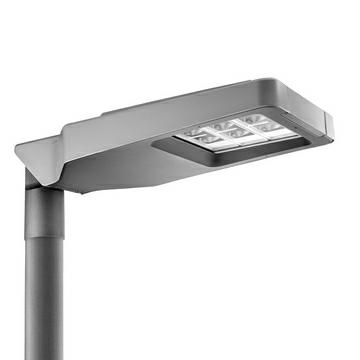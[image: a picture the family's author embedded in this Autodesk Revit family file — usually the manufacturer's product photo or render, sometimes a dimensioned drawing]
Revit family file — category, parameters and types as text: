
# Revit family: Lighting-StreetLighting-GEWISS-ROAD[5]MEDIUM-LED_OPTIC_HUGE_CLII
name_source: partatom
category: Apparecchi per illuminazione
units: mm (PartAtom-declared; Revit-internal decimal feet)

## family parameters
Basato su piano di lavoro = No
Condiviso = No
Punto di calcolo locali = No
Quota connettore circolare = Usa diametro
Sempre verticale = Sì
Sorgente d'illuminazione = No
Taglio con vuoti quando caricato = No
Tipo di parte = Normale

## types (65) — shared parameters
Applicazione = External
Catalogue = LIGHTING
IDF = edd43bf0-fde5-4ceb-9c5d-851512cf025d
IDT = ab01e1b5e8824c1da94a21a5ceb91f42
IP degree = IP66
Immagine tipo = GWR5276M.jpg
Insulation class = II
Lampada = LED
Produttore = GEWISS S.p.A.
Shock resistance = IK08
Technical sheet = https://www.gewiss.com
URL = https://www.gewiss.com
Version file RFA = 20.11
Warranty = 5 years

## per-type parameters (varying)
- GWR5174B - ROAD5 MEDI HUGE 4M 4000K 0,7A CL2 BIREG: Catalogue Range=ROAD [5]; Colour temperature=4000 K (CRI 70); Colour temperature:=4000 K (CRI 70); Descrizione=ROAD 5 BI-POW.4M 4000K 700mA OPT.ST1; EAN code=8011564858022; Electrocod=244C; LED LifeTime (L80B05)=77000H; LED current.=0,7A; Lamp-=LED; Lumen output (lm)=9190; Maximum surface exposed to the wind=0,19M2; Minimum distance from the illuminated object=1M; Modello=GWR5174B; No. Chorus modules=4 (4x3 LED); Nominal flux (lm)=12480; Number of modules=4 (4x3 LED); Operating temperature:=-25 +50 °C; Optic=H - ULOR: 0%; Overvoltage resistance=12 KV (Common and dfferential mode); Pilot current=0,7A; Power supply operation=Bi power; SEO=Street lighting; System power=108W; Tilt adjustable=-20° ÷ +10° side bracket - -10° ÷ +20° pole head; Tipo alimentatore=Constant Current Driver Led; Tipologia=Bi power; Voltage-=220/240 V - 50/60 Hz - Bi-power with self-learning; Weight (kg)=8,4; Weight (kg):=8,4; Working temperature=-25 +50 °C
- GWR5116B - ROAD5 MEDI HUGE 6M 4000K 0,85A CL2 BIREG: Catalogue Range=ROAD [5]; Colour temperature=4000 K (CRI 70); Colour temperature:=4000 K (CRI 70); Descrizione=ROAD 5 BI-POW.6M 4000K 0,85A OPT.ST1; EAN code=8011564858077; Electrocod=244C; LED LifeTime (L80B05)=120000H; LED current.=0,85A; Lamp-=LED; Lumen output (lm)=17160; Maximum surface exposed to the wind=0,19M2; Minimum distance from the illuminated object=1M; Modello=GWR5116B; No. Chorus modules=6 (6x3 LED); Nominal flux (lm)=24330; Number of modules=6 (6x3 LED); Operating temperature:=-25 +40 °C; Optic=H - ULOR: 0%; Overvoltage resistance=12 KV (Common and dfferential mode); Pilot current=0,85A; Power supply operation=Bi power; SEO=Street lighting; System power=187W; Tilt adjustable=-20° ÷ +10° side bracket - -10° ÷ +20° pole head; Tipo alimentatore=Constant Current Driver Led; Tipologia=Bi power; Voltage-=220/240 V - 50/60 Hz - Bi-power with self-learning; Weight (kg)=9.1; Weight (kg):=9,1; Working temperature=-25 +40 °C
- GWR511530K - ROAD5 MEDI HUGE 5M 3000K 0,85A CL2: Body=Die-cast aluminium -; Catalogue Range=ROAD [5]; Classification:=-; Color Rendering Index=CRI-70; Colore=Graphite grey; Colour :=Powder coating; Colour temperature=3000K; Colour temperature:=3000 K (CRI>80); Context=Street and parking lighting; Control System=Stand alone; DIN 18032-3 certification=-; Descrizione=GWR511530K - ROAD5 MEDI HUGE 5M 3000K 0,85A CL2; Device with reduced surface temperature=-; Driver=Included; Driver Box=Built-in; Efficiency (lm/W)=96; Electrocod=244C; Eletrical and lighting features=-; External screw=Stainless steel; Fixing=Pole Head - Outreach; Gasket=Anti-aging silicone; General information=-; Glow Wire Test :=-; IPEA=ROAD = B // LARGE AREAS = A ++ // CYCLOPEDONALS = B // GREEN AREAS = B // HISTORICAL CENTER = A3 +; Installationa and maintenance=-; LED Life Time (L80B05)=120000H; LED Maintenance=Not available; LED current.=0,849999999999999A; Lamp-=LED; Lifetime=L90B10 (Tq+25°C) = 100.000 h - L90B10 (Tq+40°C) = 50.000 h; Locking Hook=Integrated front handle; Lumen output (lm)=15300; Luminaire=LED Road Equipment; Materials=-; Maximum surface exposed to the wind=0,19M2; Maximum surface exposed to the wind :=0.19 m2; Minimum distance from the illuminated object=1M; Modello=GWR511530K; Mouting and installation=Pole Head - Outreach; Nominal flux (lm)=18423; Number of modules=5 (5x3 LED); Operating temperature :=-25 +40 °C; Operating temperature:=-25 +40 °C; Optic=HUGE; Optic :=Metallized polycarbonate reflector; Optic Maintenance=Not available; Optic and illuminating features=-; Overvoltage protection=DM 10KV / CM 10KV; Overvoltage resistance :=Common and dfferential mode: 10KV; Photobiological Risk Class=RG0; Rated frequency (Hz)=50 / 60; SEO=Street lighting; Shield type=4mm thick flat tempered glass; Standard Deviation Colour Matching=SDCM = 5; Standard-=EN 60598-2-3, EN 60598-1 IEC/TR 62778; Standards and approvals=-; Stocking temperature=-; Supply voltage=220 - 240 V; System power=159W; System power :=159 W @ 0.85A; Tilt adjustable=-20° ÷ +10° side bracket - -10° ÷ +20° pole head; Tilt-=-20° ÷ +10° side bracket - -10° ÷ +20° pole head; Tipo alimentatore=Constant Current Driver Led; Tipologia=Stand alone; Type of light source=LED - Not replaceable; Unified Glare Rating=G*3 - ULOR = 0; Unique digital code (Datamatrix)=Currently not present; Voltage-=220/240 V - 50/60 Hz - Stand alone; Weight (kg):=8,8; Wiring=Isolating switch
- GWR5174 - ROAD5 MEDI HUGE 4M 4000K 0,7A CL2: Catalogue Range=ROAD [5]; Colour temperature=4000 K (CRI 70); Colour temperature:=4000 K (CRI 70); Descrizione=ROAD 5 4M 4000K 700mA OPT.ST1; EAN code=8011564857940; Electrocod=244C; LED LifeTime (L80B05)=77000H; LED current.=0,7A; Lamp-=LED; Lumen output (lm)=9190; Maximum surface exposed to the wind=0,19M2; Minimum distance from the illuminated object=1M; Modello=GWR5174; No. Chorus modules=4 (4x3 LED); Nominal flux (lm)=12480; Number of modules=4 (4x3 LED); Operating temperature:=-25 +50 °C; Optic=H - ULOR: 0%; Overvoltage resistance=12 KV (Common and dfferential mode); Pilot current=0,7A; SEO=Street lighting; System power=106W; Tilt adjustable=-20° ÷ +10° side bracket - -10° ÷ +20° pole head; Tipo alimentatore=Constant Current Driver Led; Tipologia=Stand alone; Voltage-=220/240 V - 50/60 Hz - Stand alone; Weight (kg)=8,4; Weight (kg):=8,4; Working temperature=-25 +50 °C
- GWR5155B - ROAD5 MEDI HUGE 5M 4000K 0,5A CL2 BIREG: Body=Die-cast aluminium -; Catalogue Range=ROAD [5]; Classification:=-; Color Rendering Index=CRI-70; Colore=Graphite grey; Colour :=Powder coating; Colour temperature=4000K; Colour temperature:=4000 K (CRI>70); Context=Street and parking lighting; Control System=Bi-power with self-learning; DIN 18032-3 certification=-; Descrizione=GWR5155B - ROAD5 MEDI HUGE 5M 4000K 0,5A CL2 BIREG; Device with reduced surface temperature=-; Driver=Included; Driver Box=Built-in; Efficiency (lm/W)=117; Electrocod=244C; Eletrical and lighting features=-; External screw=Stainless steel; Fixing=Pole Head - Outreach; Gasket=Anti-aging silicone; General information=-; Glow Wire Test :=-; IPEA=ROAD = A3 + // LARGE AREAS = A5 + // CYCLOPEDONALS = A ++ // GREEN AREAS = A ++ // HISTORICAL CENTER = A6 +; Installationa and maintenance=-; LED Life Time (L80B05)=120000H; LED Maintenance=Not available; LED current.=0,5A; Lamp-=LED; Lifetime=L90B10 (Tq+25°C) = 100.000 h - L90B10 (Tq+50°C) = 50.000 h; Locking Hook=Integrated front handle; Lumen output (lm)=11000; Luminaire=LED Road Equipment; Materials=-; Maximum surface exposed to the wind=0,19M2; Maximum surface exposed to the wind :=0.19 m2; Minimum distance from the illuminated object=1M; Modello=GWR5155B; Mouting and installation=Pole Head - Outreach; Nominal flux (lm)=12000; Number of modules=5 (5x3 LED); Operating temperature :=-25 +50 °C; Operating temperature:=-25 +40 °C; Optic=HUGE; Optic :=Metallized polycarbonate reflector; Optic Maintenance=Not available; Optic and illuminating features=-; Overvoltage protection=DM 10KV / CM 10KV; Photobiological Risk Class=RG0; Power supply operation=Bi power; Rated frequency (Hz)=50 / 60; SEO=Street lighting; Shield type=4mm thick flat tempered glass; Standard Deviation Colour Matching=SDCM = 5; Standard-=EN 60598-2-3, EN 60598-1 IEC/TR 62778; Standards and approvals=-; Stocking temperature=-; Supply voltage=220 - 240 V; System power=91W; System power :=94 W @ 0.5A; Tilt adjustable=-20° ÷ +10° side bracket - -10° ÷ +20° pole head; Tilt-=-20° ÷ +10° side bracket - -10° ÷ +20° pole head; Type of light source=LED - Not replaceable; Unified Glare Rating=G*3 - ULOR = 0; Unique digital code (Datamatrix)=Currently not present; Voltage-=220/240 V - 50/60 Hz - Bi-power with self-learning; Weight (kg):=8,8; Wiring=Isolating switch
- GWR5176M - ROAD5 MEDI HUGE 6M 4000K 0,7A CL2 1-10V: Catalogue Range=ROAD [5]; Colour temperature=4000 K (CRI 70); Colour temperature:=4000 K (CRI 70); Descrizione=ROAD 5 DIMM.6M 4000K 700mA OPT.ST1; EAN code=8011564858244; Electrocod=244C; LED LifeTime (L80B05)=77000H; LED current.=0,7A; Lamp-=LED; Lumen output (lm)=13780; Maximum surface exposed to the wind=0,19M2; Minimum distance from the illuminated object=1M; Modello=GWR5176M; No. Chorus modules=6 (6x3 LED); Nominal flux (lm)=18720; Number of modules=6 (6x3 LED); Operating temperature:=-25 +50 °C; Optic=H - ULOR: 0%; Overvoltage resistance=12 KV (Common and dfferential mode); Pilot current=0,7A; Power supply operation=Dimmable; SEO=Street lighting; System power=159W; Tilt adjustable=-20° ÷ +10° side bracket - -10° ÷ +20° pole head; Tipo alimentatore=Constant Current Driver Led; Tipologia=Dimmable; Voltage-=220/240 V - 50/60 Hz - Dimmable 1-10 V; Weight (kg)=9.1; Weight (kg):=9,1; Working temperature=-25 +50 °C
- GWR5113B30K - ROAD5 MEDI HUGE 3M 3000K 1,0A CL2 BIREG: Body=Die-cast aluminium -; Catalogue Range=ROAD [5]; Classification:=-; Color Rendering Index=CRI-70; Colore=Graphite grey; Colour :=Powder coating; Colour temperature=3000K; Colour temperature:=3000 K (CRI>80); Context=Street and parking lighting; Control System=Bi-power with self-learning; DIN 18032-3 certification=-; Descrizione=GWR5113B30K - ROAD5 MEDI HUGE 3M 3000K 1,0A CL2 BIREG; Device with reduced surface temperature=-; Driver=Included; Driver Box=Built-in; Efficiency (lm/W)=91; Electrocod=244C; Eletrical and lighting features=-; External screw=Stainless steel; Fixing=Pole Head - Outreach; Gasket=Anti-aging silicone; General information=-; Glow Wire Test :=-; IPEA=ROAD = A // LARGE AREAS = A ++ // CYCLOPEDONALS = B // GREEN AREAS = B // HISTORICAL CENTER = A3 +; Installationa and maintenance=-; LED Life Time (L80B05)=120000H; LED Maintenance=Not available; LED current.=1A; Lamp-=LED; Lifetime=L90B10 (Tq+25°C) = 100.000 h - L90B10 (Tq+40°C) = 75.000 h; Locking Hook=Integrated front handle; Lumen output (lm)=10500; Luminaire=LED Road Equipment; Materials=-; Maximum surface exposed to the wind=0,19M2; Maximum surface exposed to the wind :=0.19 m2; Minimum distance from the illuminated object=1M; Modello=GWR5113B30K; Mouting and installation=Pole Head - Outreach; Nominal flux (lm)=12420; Number of modules=3 (3x3 LED); Operating temperature :=-25 +40 °C; Operating temperature:=-25 +40 °C; Optic=HUGE; Optic :=Metallized polycarbonate reflector; Optic Maintenance=Not available; Optic and illuminating features=-; Overvoltage protection=DM 10KV / CM 10KV; Overvoltage resistance :=Common and dfferential mode: 10KV; Photobiological Risk Class=RG0; Power supply operation=Bi power; Rated frequency (Hz)=50 / 60; SEO=Street lighting; Shield type=4mm thick flat tempered glass; Standard Deviation Colour Matching=SDCM = 5; Standard-=EN 60598-2-3, EN 60598-1 IEC/TR 62778; Standards and approvals=-; Stocking temperature=-; Supply voltage=220 - 240 V; System power=115W; System power :=115 W @ 1A; Tilt adjustable=-20° ÷ +10° side bracket - -10° ÷ +20° pole head; Tilt-=-20° ÷ +10° side bracket - -10° ÷ +20° pole head; Tipo alimentatore=Constant Current Driver Led; Tipologia=Bi power; Type of light source=LED - Not replaceable; Unified Glare Rating=G*3 - ULOR = 0; Unique digital code (Datamatrix)=Currently not present; Voltage-=220/240 V - 50/60 Hz - Bi-power with self-learning; Weight (kg):=8; Wiring=Isolating switch
- GWR511630K - ROAD5 MEDI HUGE 6M 3000K 0,85A CL2: Body=Die-cast aluminium -; Catalogue Range=ROAD [5]; Classification:=-; Color Rendering Index=CRI-70; Colore=Graphite grey; Colour :=Powder coating; Colour temperature=3000K; Colour temperature:=3000 K (CRI>80); Context=Street and parking lighting; Control System=Stand alone; DIN 18032-3 certification=-; Descrizione=GWR511630K - ROAD5 MEDI HUGE 6M 3000K 0,85A CL2; Device with reduced surface temperature=-; Driver=Included; Driver Box=Built-in; Efficiency (lm/W)=99; Electrocod=244C; Eletrical and lighting features=-; External screw=Stainless steel; Fixing=Pole Head - Outreach; Gasket=Anti-aging silicone; General information=-; Glow Wire Test :=-; IPEA=ROAD = B // LARGE AREAS = A ++ // CYCLOPEDONALS = A // GREEN AREAS = A // HISTORICAL CENTER = A3 +; Installationa and maintenance=-; LED Life Time (L80B05)=120000H; LED Maintenance=Not available; LED current.=0,849999999999999A; Lamp-=LED; Lifetime=L90B10 (Tq+25°C) = 100.000 h - L90B10 (Tq+40°C) = 50.000 h; Locking Hook=Integrated front handle; Lumen output (lm)=18400; Luminaire=LED Road Equipment; Materials=-; Maximum surface exposed to the wind=0,19M2; Maximum surface exposed to the wind :=0.19 m2; Minimum distance from the illuminated object=1M; Modello=GWR511630K; Mouting and installation=Pole Head - Outreach; Nominal flux (lm)=21114; Number of modules=6 (6x3 LED); Operating temperature :=-25 +40 °C; Operating temperature:=-25 +40 °C; Optic=HUGE; Optic :=Metallized polycarbonate reflector; Optic Maintenance=Not available; Optic and illuminating features=-; Overvoltage protection=DM 10KV / CM 10KV; Overvoltage resistance :=Common and dfferential mode: 10KV; Photobiological Risk Class=RG0; Rated frequency (Hz)=50 / 60; SEO=Street lighting; Shield type=4mm thick flat tempered glass; Standard Deviation Colour Matching=SDCM = 5; Standard-=EN 60598-2-3, EN 60598-1 IEC/TR 62778; Standards and approvals=-; Stocking temperature=-; Supply voltage=220 - 240 V; System power=185W; System power :=185 W @ 0.85A; Tilt adjustable=-20° ÷ +10° side bracket - -10° ÷ +20° pole head; Tilt-=-20° ÷ +10° side bracket - -10° ÷ +20° pole head; Tipo alimentatore=Constant Current Driver Led; Tipologia=Stand alone; Type of light source=LED - Not replaceable; Unified Glare Rating=G*3 - ULOR = 0; Unique digital code (Datamatrix)=Currently not present; Voltage-=220/240 V - 50/60 Hz - Stand alone; Weight (kg):=9,09999999999999; Wiring=Isolating switch
- GWR5114B - ROAD5 MEDI HUGE 4M 4000K 1,0A CL2 BIREG: Catalogue Range=ROAD [5]; Colour temperature=4000 K (CRI 70); Colour temperature:=4000 K (CRI 70); Descrizione=ROAD 5 BI-POW.4M 4000K 1A OPT.ST1; EAN code=8011564858039; Electrocod=244C; LED LifeTime (L80B05)=120000H; LED current.=1A; Lamp-=LED; Lumen output (lm)=13460; Maximum surface exposed to the wind=0,19M2; Minimum distance from the illuminated object=1M; Modello=GWR5114B; No. Chorus modules=4 (4x3 LED); Nominal flux (lm)=19080; Number of modules=4 (4x3 LED); Operating temperature:=-25 +40 °C; Optic=H - ULOR: 0%; Overvoltage resistance=12 KV (Common and dfferential mode); Pilot current=1A; Power supply operation=Bi power; SEO=Street lighting; System power=153W; Tilt adjustable=-20° ÷ +10° side bracket - -10° ÷ +20° pole head; Tipo alimentatore=Constant Current Driver Led; Tipologia=Bi power; Voltage-=220/240 V - 50/60 Hz - Bi-power with self-learning; Weight (kg)=8,4; Weight (kg):=8,4; Working temperature=-25 +40 °C
- GWR5175 - ROAD5 MEDI HUGE 5M 4000K 0,7A CL2: Catalogue Range=ROAD [5]; Colour temperature=4000 K (CRI 70); Colour temperature:=4000 K (CRI 70); Descrizione=ROAD 5 5M 4000K 700mA OPT.ST1; EAN code=8011564857964; Electrocod=244C; LED LifeTime (L80B05)=77000H; LED current.=0,7A; Lamp-=LED; Lumen output (lm)=11480; Maximum surface exposed to the wind=0,19M2; Minimum distance from the illuminated object=1M; Modello=GWR5175; No. Chorus modules=5 (5x3 LED); Nominal flux (lm)=15600; Number of modules=5 (5x3 LED); Operating temperature:=-25 +50 °C; Optic=H - ULOR: 0%; Overvoltage resistance=12 KV (Common and dfferential mode); Pilot current=0,7A; SEO=Street lighting; System power=132W; Tilt adjustable=-20° ÷ +10° side bracket - -10° ÷ +20° pole head; Tipo alimentatore=Constant Current Driver Led; Tipologia=Stand alone; Voltage-=220/240 V - 50/60 Hz - Stand alone; Weight (kg)=8,8; Weight (kg):=8,8; Working temperature=-25 +50 °C
- GWR5156M - ROAD5 MEDI HUGE 6M 4000K 0,5A CL2 1-10V: Body=Die-cast aluminium -; Catalogue Range=ROAD [5]; Classification:=-; Color Rendering Index=CRI-70; Colore=Graphite grey; Colour :=Powder coating; Colour temperature=4000K; Colour temperature:=4000 K (CRI>70); Context=Street and parking lighting; Control System=Dimmable 1-10 V; DIN 18032-3 certification=-; Descrizione=GWR5156M - ROAD5 MEDI HUGE 6M 4000K 0,5A CL2 1-10V; Device with reduced surface temperature=-; Driver=Included; Driver Box=Built-in; Efficiency (lm/W)=117; Electrocod=244C; Eletrical and lighting features=-; External screw=Stainless steel; Fixing=Pole Head - Outreach; Gasket=Anti-aging silicone; General information=-; Glow Wire Test :=-; IPEA=ROAD = A3 + // LARGE AREAS = A5 + // CYCLOPEDONALS = A ++ // GREEN AREAS = A ++ // HISTORICAL CENTER = A6 +; Installationa and maintenance=-; LED Life Time (L80B05)=120000H; LED Maintenance=Not available; LED current.=0,5A; Lamp-=LED; Lifetime=L90B10 (Tq+25°C) = 100.000 h - L90B10 (Tq+50°C) = 50.000 h; Locking Hook=Integrated front handle; Lumen output (lm)=13200; Luminaire=LED Road Equipment; Materials=-; Maximum surface exposed to the wind=0,19M2; Maximum surface exposed to the wind :=0.19 m2; Minimum distance from the illuminated object=1M; Modello=GWR5156M; Mouting and installation=Pole Head - Outreach; Nominal flux (lm)=14400; Number of modules=6 (6x3 LED); Operating temperature :=-25 +50 °C; Operating temperature:=-25 +40 °C; Optic=HUGE; Optic :=Metallized polycarbonate reflector; Optic Maintenance=Not available; Optic and illuminating features=-; Overvoltage protection=DM 10KV / CM 10KV; Photobiological Risk Class=RG0; Rated frequency (Hz)=50 / 60; SEO=Street lighting; Shield type=4mm thick flat tempered glass; Standard Deviation Colour Matching=SDCM = 5; Standard-=EN 60598-2-3, EN 60598-1 IEC/TR 62778; Standards and approvals=-; Stocking temperature=-; Supply voltage=220 - 240 V; System power=109W; System power :=113 W @ 0.5A; Tilt adjustable=-20° ÷ +10° side bracket - -10° ÷ +20° pole head; Tilt-=-20° ÷ +10° side bracket - -10° ÷ +20° pole head; Tipologia=Dimmable; Type of light source=LED - Not replaceable; Unified Glare Rating=G*3 - ULOR = 0; Unique digital code (Datamatrix)=Currently not present; Voltage-=220/240 V - 50/60 Hz - Dimmable 1-10 V; Weight (kg):=9,09999999999999; Wiring=Isolating switch
- GWR5173M - ROAD5 MEDI HUGE 3M 4000K 0,7A CL2 1-10V: Catalogue Range=ROAD [5]; Colour temperature=4000 K (CRI 70); Colour temperature:=4000 K (CRI 70); Descrizione=ROAD 5 DIMM.3M 4000K 700mA OPT.ST1; EAN code=8011564858084; Electrocod=244C; LED LifeTime (L80B05)=77000H; LED current.=0,7A; Lamp-=LED; Lumen output (lm)=6890; Maximum surface exposed to the wind=0,19M2; Minimum distance from the illuminated object=1M; Modello=GWR5173M; No. Chorus modules=3 (3x3 LED); Nominal flux (lm)=9360; Number of modules=3 (3x3 LED); Operating temperature:=-25 +50 °C; Optic=H - ULOR: 0%; Overvoltage resistance=12 KV (Common and dfferential mode); Pilot current=0,7A; Power supply operation=Dimmable; SEO=Street lighting; System power=79W; Tilt adjustable=-20° ÷ +10° side bracket - -10° ÷ +20° pole head; Tipo alimentatore=Constant Current Driver Led; Tipologia=Dimmable; Voltage-=220/240 V - 50/60 Hz - Dimmable 1-10 V; Weight (kg)=8; Weight (kg):=8; Working temperature=-25 +50 °C
- GWR5174M30K - ROAD5 MEDI HUGE 4M 3000K 0,7A CL2 1-10V: Body=Die-cast aluminium -; Catalogue Range=ROAD [5]; Classification:=-; Color Rendering Index=CRI-70; Colore=Graphite grey; Colour :=Powder coating; Colour temperature=3000K; Colour temperature:=3000 K (CRI>80); Context=Street and parking lighting; Control System=Dimmable 1-10 V; DIN 18032-3 certification=-; Descrizione=GWR5174M30K - ROAD5 MEDI HUGE 4M 3000K 0,7A CL2 1-10V; Device with reduced surface temperature=-; Driver=Included; Driver Box=Built-in; Efficiency (lm/W)=96; Electrocod=244C; Eletrical and lighting features=-; External screw=Stainless steel; Fixing=Pole Head - Outreach; Gasket=Anti-aging silicone; General information=-; Glow Wire Test :=-; IPEA=ROAD = A // LARGE AREAS = A ++ // CYCLOPEDONALS = A // GREEN AREAS = A // HISTORICAL CENTER = A3 +; Installationa and maintenance=-; LED Life Time (L80B05)=77000H; LED Maintenance=Not available; LED current.=0,7A; Lamp-=LED; Lifetime=L90B10 (Tq+25°C) = 100.000 h - L90B10 (Tq+50°C) = 50.000 h; Locking Hook=Integrated front handle; Lumen output (lm)=10400; Luminaire=LED Road Equipment; Materials=-; Maximum surface exposed to the wind=0,19M2; Maximum surface exposed to the wind :=0.19 m2; Minimum distance from the illuminated object=1M; Modello=GWR5174M30K; Mouting and installation=Pole Head - Outreach; Nominal flux (lm)=10800; Number of modules=4 (4x3 LED); Operating temperature :=-25 +50 °C; Operating temperature:=-25 +50 °C; Optic=HUGE; Optic :=Metallized polycarbonate reflector; Optic Maintenance=Not available; Optic and illuminating features=-; Overvoltage protection=DM 10KV / CM 10KV; Overvoltage resistance :=Common and dfferential mode: 10KV; Photobiological Risk Class=RG0; Power supply operation=Dimmable; Rated frequency (Hz)=50 / 60; SEO=Street lighting; Shield type=4mm thick flat tempered glass; Standard Deviation Colour Matching=SDCM = 5; Standard-=EN 60598-2-3, EN 60598-1 IEC/TR 62778; Standards and approvals=-; Stocking temperature=-; Supply voltage=220 - 240 V; System power=106W; System power :=108 W @ 0.7A; Tilt adjustable=-20° ÷ +10° side bracket - -10° ÷ +20° pole head; Tilt-=-20° ÷ +10° side bracket - -10° ÷ +20° pole head; Tipo alimentatore=Constant Current Driver Led; Tipologia=Dimmable; Type of light source=LED - Not replaceable; Unified Glare Rating=G*3 - ULOR = 0; Unique digital code (Datamatrix)=Currently not present; Voltage-=220/240 V - 50/60 Hz - Dimmable 1-10 V; Weight (kg):=8,4; Wiring=Isolating switch
- GWR5176V - ROAD5 MEDI HUGE V 6M 4000K 0,7A CL2: Body=Die-cast aluminium -; Catalogue Range=ROAD [5]; Classification:=-; Color Rendering Index=CRI-70; Colore=Graphite grey; Colour :=Powder coating; Colour temperature=4000K; Colour temperature:=4000 K (CRI>70); Context=Street and parking lighting; Control System=DALI - 5 Step; DIN 18032-3 certification=-; Descrizione=GWR5176V - ROAD5 MEDI HUGE V 6M 4000K 0,7A CL2; Device with reduced surface temperature=-; Driver=Included; Driver Box=Built-in; Efficiency (lm/W)=111; Electrocod=244C; Eletrical and lighting features=-; External screw=Stainless steel; Fixing=Pole Head - Outreach; Gasket=Anti-aging silicone; General information=-; Glow Wire Test :=-; IPEA=ROAD = A + // LARGE AREAS = A4 + // CYCLOPEDONALS = A + // GREEN AREAS = A + // HISTORICAL CENTER = A6 +; Installationa and maintenance=-; LED Life Time (L80B05)=120000H; LED Maintenance=Not available; LED current.=0,7A; Lamp-=LED; Lifetime=L90B10 (Tq+25°C) = 100.000 h - L90B10 (Tq+50°C) = 50.000 h; Locking Hook=Integrated front handle; Lumen output (lm)=17900; Luminaire=LED Road Equipment; Materials=-; Maximum surface exposed to the wind=0,19M2; Maximum surface exposed to the wind :=0.19 m2; Minimum distance from the illuminated object=1M; Modello=GWR5176V; Mouting and installation=Pole Head - Outreach; Nominal flux (lm)=18720; Number of modules=6 (6x3 LED); Operating temperature :=-25 +50 °C; Operating temperature:=-25 +40 °C; Optic=HUGE; Optic :=Metallized polycarbonate reflector; Optic Maintenance=Not available; Optic and illuminating features=-; Overvoltage protection=DM 10KV / CM 10KV; Photobiological Risk Class=RG0; Rated frequency (Hz)=50 / 60; SEO=Street lighting; Shield type=4mm thick flat tempered glass; Standard Deviation Colour Matching=SDCM = 5; Standard-=EN 60598-2-3, EN 60598-1 IEC/TR 62778; Standards and approvals=-; Stocking temperature=-; Supply voltage=220 - 240 V; System power=159W; System power :=161 W @ 0.7A; Tilt adjustable=-20° ÷ +10° side bracket - -10° ÷ +20° pole head; Tilt-=-20° ÷ +10° side bracket - -10° ÷ +20° pole head; Tipologia=Programmable (5 step); Type of light source=LED - Not replaceable; Unified Glare Rating=G*3 - ULOR = 0; Unique digital code (Datamatrix)=Currently not present; Voltage-=220/240 V - 50/60 Hz - Stand alone and/or programmable; Weight (kg):=9,09999999999999; Wiring=Isolating switch
- GWR5173M30K - ROAD5 MEDI HUGE 3M 3000K 0,7A CL2 1-10V: Body=Die-cast aluminium -; Catalogue Range=ROAD [5]; Classification:=-; Color Rendering Index=CRI-70; Colore=Graphite grey; Colour :=Powder coating; Colour temperature=3000K; Colour temperature:=3000 K (CRI>80); Context=Street and parking lighting; Control System=Dimmable 1-10 V; DIN 18032-3 certification=-; Descrizione=GWR5173M30K - ROAD5 MEDI HUGE 3M 3000K 0,7A CL2 1-10V; Device with reduced surface temperature=-; Driver=Included; Driver Box=Built-in; Efficiency (lm/W)=96; Electrocod=244C; Eletrical and lighting features=-; External screw=Stainless steel; Fixing=Pole Head - Outreach; Gasket=Anti-aging silicone; General information=-; Glow Wire Test :=-; IPEA=ROAD = A + // LARGE AREAS = A ++ // CYCLOPEDONALS = A + // GREEN AREAS = A + // HISTORICAL CENTER = A5 +; Installationa and maintenance=-; LED Life Time (L80B05)=77000H; LED Maintenance=Not available; LED current.=0,7A; Lamp-=LED; Lifetime=L90B10 (Tq+25°C) = 100.000 h - L90B10 (Tq+50°C) = 75.000 h; Locking Hook=Integrated front handle; Lumen output (lm)=7800; Luminaire=LED Road Equipment; Materials=-; Maximum surface exposed to the wind=0,19M2; Maximum surface exposed to the wind :=0.19 m2; Minimum distance from the illuminated object=1M; Modello=GWR5173M30K; Mouting and installation=Pole Head - Outreach; Nominal flux (lm)=8100; Number of modules=3 (3x3 LED); Operating temperature :=-25 +50 °C; Operating temperature:=-25 +50 °C; Optic=HUGE; Optic :=Metallized polycarbonate reflector; Optic Maintenance=Not available; Optic and illuminating features=-; Overvoltage protection=DM 10KV / CM 10KV; Overvoltage resistance :=Common and dfferential mode: 10KV; Photobiological Risk Class=RG0; Power supply operation=Dimmable; Rated frequency (Hz)=50 / 60; SEO=Street lighting; Shield type=4mm thick flat tempered glass; Standard Deviation Colour Matching=SDCM = 5; Standard-=EN 60598-2-3, EN 60598-1 IEC/TR 62778; Standards and approvals=-; Stocking temperature=-; Supply voltage=220 - 240 V; System power=79W; System power :=81 W @ 0.7A; Tilt adjustable=-20° ÷ +10° side bracket - -10° ÷ +20° pole head; Tilt-=-20° ÷ +10° side bracket - -10° ÷ +20° pole head; Tipo alimentatore=Constant Current Driver Led; Tipologia=Dimmable; Type of light source=LED - Not replaceable; Unified Glare Rating=G*3 - ULOR = 0; Unique digital code (Datamatrix)=Currently not present; Voltage-=220/240 V - 50/60 Hz - Dimmable 1-10 V; Weight (kg):=8; Wiring=Isolating switch
- GWR5115B30K - ROAD5 MEDI HUGE 5M 3000K 0,85A CL2 BIREG: Body=Die-cast aluminium -; Catalogue Range=ROAD [5]; Classification:=-; Color Rendering Index=CRI-70; Colore=Graphite grey; Colour :=Powder coating; Colour temperature=3000K; Colour temperature:=3000 K (CRI>80); Context=Street and parking lighting; Control System=Bi-power with self-learning; DIN 18032-3 certification=-; Descrizione=GWR5115B30K - ROAD5 MEDI HUGE 5M 3000K 0,85A CL2 BIREG; Device with reduced surface temperature=-; Driver=Included; Driver Box=Built-in; Efficiency (lm/W)=95; Electrocod=244C; Eletrical and lighting features=-; External screw=Stainless steel; Fixing=Pole Head - Outreach; Gasket=Anti-aging silicone; General information=-; Glow Wire Test :=-; IPEA=ROAD = B // LARGE AREAS = A ++ // CYCLOPEDONALS = B // GREEN AREAS = B // HISTORICAL CENTER = A3 +; Installationa and maintenance=-; LED Life Time (L80B05)=120000H; LED Maintenance=Not available; LED current.=0,849999999999999A; Lamp-=LED; Lifetime=L90B10 (Tq+25°C) = 100.000 h - L90B10 (Tq+40°C) = 50.000 h; Locking Hook=Integrated front handle; Lumen output (lm)=15300; Luminaire=LED Road Equipment; Materials=-; Maximum surface exposed to the wind=0,19M2; Maximum surface exposed to the wind :=0.19 m2; Minimum distance from the illuminated object=1M; Modello=GWR5115B30K; Mouting and installation=Pole Head - Outreach; Nominal flux (lm)=18423; Number of modules=5 (5x3 LED); Operating temperature :=-25 +40 °C; Operating temperature:=-25 +40 °C; Optic=HUGE; Optic :=Metallized polycarbonate reflector; Optic Maintenance=Not available; Optic and illuminating features=-; Overvoltage protection=DM 10KV / CM 10KV; Overvoltage resistance :=Common and dfferential mode: 10KV; Photobiological Risk Class=RG0; Power supply operation=Bi power; Rated frequency (Hz)=50 / 60; SEO=Street lighting; Shield type=4mm thick flat tempered glass; Standard Deviation Colour Matching=SDCM = 5; Standard-=EN 60598-2-3, EN 60598-1 IEC/TR 62778; Standards and approvals=-; Stocking temperature=-; Supply voltage=220 - 240 V; System power=161W; System power :=161 W @ 0.85A; Tilt adjustable=-20° ÷ +10° side bracket - -10° ÷ +20° pole head; Tilt-=-20° ÷ +10° side bracket - -10° ÷ +20° pole head; Tipo alimentatore=Constant Current Driver Led; Tipologia=Bi power; Type of light source=LED - Not replaceable; Unified Glare Rating=G*3 - ULOR = 0; Unique digital code (Datamatrix)=Currently not present; Voltage-=220/240 V - 50/60 Hz - Bi-power with self-learning; Weight (kg):=8,8; Wiring=Isolating switch
- GWR5176B - ROAD5 MEDI HUGE 6M 4000K 0,7A CL2 BIREG: Catalogue Range=ROAD [5]; Colour temperature=4000 K (CRI 70); Colour temperature:=4000 K (CRI 70); Descrizione=ROAD 5 BI-POW.6M 4000K 700mA OPT.ST1; EAN code=8011564858060; Electrocod=244C; LED LifeTime (L80B05)=77000H; LED current.=0,7A; Lamp-=LED; Lumen output (lm)=13780; Maximum surface exposed to the wind=0,19M2; Minimum distance from the illuminated object=1M; Modello=GWR5176B; No. Chorus modules=6 (6x3 LED); Nominal flux (lm)=18720; Number of modules=6 (6x3 LED); Operating temperature:=-25 +50 °C; Optic=H - ULOR: 0%; Overvoltage resistance=12 KV (Common and dfferential mode); Pilot current=0,7A; Power supply operation=Bi power; SEO=Street lighting; System power=161W; Tilt adjustable=-20° ÷ +10° side bracket - -10° ÷ +20° pole head; Tipo alimentatore=Constant Current Driver Led; Tipologia=Bi power; Voltage-=220/240 V - 50/60 Hz - Bi-power with self-learning; Weight (kg)=9.1; Weight (kg):=9,1; Working temperature=-25 +50 °C
- GWR5113 - ROAD 5 3M 4000K 1A OPT.ST1: Catalogue Range=ROAD [5]; Colour temperature=4000 K (CRI 70); Colour temperature:=4000 K (CRI 70); Descrizione=ROAD 5 3M 4000K 1A OPT.ST1; EAN code=8011564857933; Electrocod=244C; LED LifeTime (L80B05)=120000H; LED current.=1A; Lamp-=LED; Lumen output (lm)=10100; Maximum surface exposed to the wind=0,19M2; Minimum distance from the illuminated object=1M; Modello=GWR5113; No. Chorus modules=3 (3x3 LED); Nominal flux (lm)=14310; Number of modules=3 (3x3 LED); Operating temperature:=-25 +40 °C; Optic=H - ULOR: 0%; Overvoltage resistance=12 KV (Common and dfferential mode); Pilot current=1A; SEO=Street lighting; System power=113W; Tilt adjustable=-20° ÷ +10° side bracket - -10° ÷ +20° pole head; Tipo alimentatore=Constant Current Driver Led; Tipologia=Stand alone; Voltage-=220/240 V - 50/60 Hz - Stand alone; Weight (kg)=8; Weight (kg):=8; Working temperature=-25 +40 °C
- GWR5154M - ROAD5 MEDI HUGE 4M 4000K 0,5A CL2 1-10V: Body=Die-cast aluminium -; Catalogue Range=ROAD [5]; Classification:=-; Color Rendering Index=CRI-70; Colore=Graphite grey; Colour :=Powder coating; Colour temperature=4000K; Colour temperature:=4000 K (CRI>70); Context=Street and parking lighting; Control System=Dimmable 1-10 V; DIN 18032-3 certification=-; Descrizione=GWR5154M - ROAD5 MEDI HUGE 4M 4000K 0,5A CL2 1-10V; Device with reduced surface temperature=-; Driver=Included; Driver Box=Built-in; Efficiency (lm/W)=116; Electrocod=244C; Eletrical and lighting features=-; External screw=Stainless steel; Fixing=Pole Head - Outreach; Gasket=Anti-aging silicone; General information=-; Glow Wire Test :=-; IPEA=ROAD = A4 + // LARGE AREAS = A5 + // CYCLOPEDONALS = A3 + // GREEN AREAS = A3 + // HISTORICAL CENTER = A6 +; Installationa and maintenance=-; LED Life Time (L80B05)=120000H; LED Maintenance=Not available; LED current.=0,5A; Lamp-=LED; Lifetime=L90B10 (Tq+25°C) = 100.000 h - L90B10 (Tq+50°C) = 50.000 h; Locking Hook=Integrated front handle; Lumen output (lm)=8800; Luminaire=LED Road Equipment; Materials=-; Maximum surface exposed to the wind=0,19M2; Maximum surface exposed to the wind :=0.19 m2; Minimum distance from the illuminated object=1M; Modello=GWR5154M; Mouting and installation=Pole Head - Outreach; Nominal flux (lm)=9600; Number of modules=4 (4x3 LED); Operating temperature :=-25 +50 °C; Operating temperature:=-25 +40 °C; Optic=HUGE; Optic :=Metallized polycarbonate reflector; Optic Maintenance=Not available; Optic and illuminating features=-; Overvoltage protection=DM 10KV / CM 10KV; Photobiological Risk Class=RG0; Rated frequency (Hz)=50 / 60; SEO=Street lighting; Shield type=4mm thick flat tempered glass; Standard Deviation Colour Matching=SDCM = 5; Standard-=EN 60598-2-3, EN 60598-1 IEC/TR 62778; Standards and approvals=-; Stocking temperature=-; Supply voltage=220 - 240 V; System power=73W; System power :=76 W @ 0.5A; Tilt adjustable=-20° ÷ +10° side bracket - -10° ÷ +20° pole head; Tilt-=-20° ÷ +10° side bracket - -10° ÷ +20° pole head; Tipologia=Dimmable; Type of light source=LED - Not replaceable; Unified Glare Rating=G*3 - ULOR = 0; Unique digital code (Datamatrix)=Currently not present; Voltage-=220/240 V - 50/60 Hz - Dimmable 1-10 V; Weight (kg):=8,4; Wiring=Isolating switch
- GWR5115M - ROAD5 MEDI HUGE 5M 4000K 0,85A CL2 1-10V: Catalogue Range=ROAD [5]; Colour temperature=4000 K (CRI 70); Colour temperature:=4000 K (CRI 70); Descrizione=ROAD 5 DIMM.5M 4000K 0,85A OPT.ST1; EAN code=8011564858237; Electrocod=244C; LED LifeTime (L80B05)=120000H; LED current.=0,85A; Lamp-=LED; Lumen output (lm)=14970; Maximum surface exposed to the wind=0,19M2; Minimum distance from the illuminated object=1M; Modello=GWR5115M; No. Chorus modules=5 (5x3 LED); Nominal flux (lm)=21230; Number of modules=5 (5x3 LED); Operating temperature:=-25 +40 °C; Optic=H - ULOR: 0%; Overvoltage resistance=12 KV (Common and dfferential mode); Pilot current=0,85A; Power supply operation=Dimmable; SEO=Street lighting; System power=159W; Tilt adjustable=-20° ÷ +10° side bracket - -10° ÷ +20° pole head; Tipo alimentatore=Constant Current Driver Led; Tipologia=Dimmable; Voltage-=220/240 V - 50/60 Hz - Dimmable 1-10 V; Weight (kg)=8,8; Weight (kg):=8,8; Working temperature=-25 +40 °C
- GWR5174B30K - ROAD5 MEDI HUGE 4M 3000K 0,7A CL2 BIREG: Body=Die-cast aluminium -; Catalogue Range=ROAD [5]; Classification:=-; Color Rendering Index=CRI-70; Colore=Graphite grey; Colour :=Powder coating; Colour temperature=3000K; Colour temperature:=3000 K (CRI>80); Context=Street and parking lighting; Control System=Bi-power with self-learning; DIN 18032-3 certification=-; Descrizione=GWR5174B30K - ROAD5 MEDI HUGE 4M 3000K 0,7A CL2 BIREG; Device with reduced surface temperature=-; Driver=Included; Driver Box=Built-in; Efficiency (lm/W)=96; Electrocod=244C; Eletrical and lighting features=-; External screw=Stainless steel; Fixing=Pole Head - Outreach; Gasket=Anti-aging silicone; General information=-; Glow Wire Test :=-; IPEA=ROAD = A // LARGE AREAS = A ++ // CYCLOPEDONALS = A // GREEN AREAS = A // HISTORICAL CENTER = A3 +; Installationa and maintenance=-; LED Life Time (L80B05)=77000H; LED Maintenance=Not available; LED current.=0,7A; Lamp-=LED; Lifetime=L90B10 (Tq+25°C) = 100.000 h - L90B10 (Tq+50°C) = 50.000 h; Locking Hook=Integrated front handle; Lumen output (lm)=10400; Luminaire=LED Road Equipment; Materials=-; Maximum surface exposed to the wind=0,19M2; Maximum surface exposed to the wind :=0.19 m2; Minimum distance from the illuminated object=1M; Modello=GWR5174B30K; Mouting and installation=Pole Head - Outreach; Nominal flux (lm)=10800; Number of modules=4 (4x3 LED); Operating temperature :=-25 +50 °C; Operating temperature:=-25 +50 °C; Optic=HUGE; Optic :=Metallized polycarbonate reflector; Optic Maintenance=Not available; Optic and illuminating features=-; Overvoltage protection=DM 10KV / CM 10KV; Overvoltage resistance :=Common and dfferential mode: 10KV; Photobiological Risk Class=RG0; Power supply operation=Bi power; Rated frequency (Hz)=50 / 60; SEO=Street lighting; Shield type=4mm thick flat tempered glass; Standard Deviation Colour Matching=SDCM = 5; Standard-=EN 60598-2-3, EN 60598-1 IEC/TR 62778; Standards and approvals=-; Stocking temperature=-; Supply voltage=220 - 240 V; System power=108W; System power :=108 W @ 0.7A; Tilt adjustable=-20° ÷ +10° side bracket - -10° ÷ +20° pole head; Tilt-=-20° ÷ +10° side bracket - -10° ÷ +20° pole head; Tipo alimentatore=Constant Current Driver Led; Tipologia=Bi power; Type of light source=LED - Not replaceable; Unified Glare Rating=G*3 - ULOR = 0; Unique digital code (Datamatrix)=Currently not present; Voltage-=220/240 V - 50/60 Hz - Bi-power with self-learning; Weight (kg):=8,4; Wiring=Isolating switch
- GWR5173B30K - ROAD5 MEDI HUGE 3M 3000K 0,7A CL2 BIREG: Body=Die-cast aluminium -; Catalogue Range=ROAD [5]; Classification:=-; Color Rendering Index=CRI-70; Colore=Graphite grey; Colour :=Powder coating; Colour temperature=3000K; Colour temperature:=3000 K (CRI>80); Context=Street and parking lighting; Control System=Bi-power with self-learning; DIN 18032-3 certification=-; Descrizione=GWR5173B30K - ROAD5 MEDI HUGE 3M 3000K 0,7A CL2 BIREG; Device with reduced surface temperature=-; Driver=Included; Driver Box=Built-in; Efficiency (lm/W)=96; Electrocod=244C; Eletrical and lighting features=-; External screw=Stainless steel; Fixing=Pole Head - Outreach; Gasket=Anti-aging silicone; General information=-; Glow Wire Test :=-; IPEA=ROAD = A + // LARGE AREAS = A ++ // CYCLOPEDONALS = A + // GREEN AREAS = A + // HISTORICAL CENTER = A5 +; Installationa and maintenance=-; LED Life Time (L80B05)=77000H; LED Maintenance=Not available; LED current.=0,7A; Lamp-=LED; Lifetime=L90B10 (Tq+25°C) = 100.000 h - L90B10 (Tq+50°C) = 75.000 h; Locking Hook=Integrated front handle; Lumen output (lm)=7800; Luminaire=LED Road Equipment; Materials=-; Maximum surface exposed to the wind=0,19M2; Maximum surface exposed to the wind :=0.19 m2; Minimum distance from the illuminated object=1M; Modello=GWR5173B30K; Mouting and installation=Pole Head - Outreach; Nominal flux (lm)=8100; Number of modules=3 (3x3 LED); Operating temperature :=-25 +50 °C; Operating temperature:=-25 +50 °C; Optic=HUGE; Optic :=Metallized polycarbonate reflector; Optic Maintenance=Not available; Optic and illuminating features=-; Overvoltage protection=DM 10KV / CM 10KV; Overvoltage resistance :=Common and dfferential mode: 10KV; Photobiological Risk Class=RG0; Power supply operation=Bi power; Rated frequency (Hz)=50 / 60; SEO=Street lighting; Shield type=4mm thick flat tempered glass; Standard Deviation Colour Matching=SDCM = 5; Standard-=EN 60598-2-3, EN 60598-1 IEC/TR 62778; Standards and approvals=-; Stocking temperature=-; Supply voltage=220 - 240 V; System power=81W; System power :=81 W @ 0.7A; Tilt adjustable=-20° ÷ +10° side bracket - -10° ÷ +20° pole head; Tilt-=-20° ÷ +10° side bracket - -10° ÷ +20° pole head; Tipo alimentatore=Constant Current Driver Led; Tipologia=Bi power; Type of light source=LED - Not replaceable; Unified Glare Rating=G*3 - ULOR = 0; Unique digital code (Datamatrix)=Currently not present; Voltage-=220/240 V - 50/60 Hz - Bi-power with self-learning; Weight (kg):=8; Wiring=Isolating switch
- GWR5154B - ROAD5 MEDI HUGE 4M 4000K 0,5A CL2 BIREG: Body=Die-cast aluminium -; Catalogue Range=ROAD [5]; Classification:=-; Color Rendering Index=CRI-70; Colore=Graphite grey; Colour :=Powder coating; Colour temperature=4000K; Colour temperature:=4000 K (CRI>70); Context=Street and parking lighting; Control System=Bi-power with self-learning; DIN 18032-3 certification=-; Descrizione=GWR5154B - ROAD5 MEDI HUGE 4M 4000K 0,5A CL2 BIREG; Device with reduced surface temperature=-; Driver=Included; Driver Box=Built-in; Efficiency (lm/W)=116; Electrocod=244C; Eletrical and lighting features=-; External screw=Stainless steel; Fixing=Pole Head - Outreach; Gasket=Anti-aging silicone; General information=-; Glow Wire Test :=-; IPEA=ROAD = A4 + // LARGE AREAS = A5 + // CYCLOPEDONALS = A3 + // GREEN AREAS = A3 + // HISTORICAL CENTER = A6 +; Installationa and maintenance=-; LED Life Time (L80B05)=120000H; LED Maintenance=Not available; LED current.=0,5A; Lamp-=LED; Lifetime=L90B10 (Tq+25°C) = 100.000 h - L90B10 (Tq+50°C) = 50.000 h; Locking Hook=Integrated front handle; Lumen output (lm)=8800; Luminaire=LED Road Equipment; Materials=-; Maximum surface exposed to the wind=0,19M2; Maximum surface exposed to the wind :=0.19 m2; Minimum distance from the illuminated object=1M; Modello=GWR5154B; Mouting and installation=Pole Head - Outreach; Nominal flux (lm)=9600; Number of modules=4 (4x3 LED); Operating temperature :=-25 +50 °C; Operating temperature:=-25 +40 °C; Optic=HUGE; Optic :=Metallized polycarbonate reflector; Optic Maintenance=Not available; Optic and illuminating features=-; Overvoltage protection=DM 10KV / CM 10KV; Photobiological Risk Class=RG0; Power supply operation=Bi power; Rated frequency (Hz)=50 / 60; SEO=Street lighting; Shield type=4mm thick flat tempered glass; Standard Deviation Colour Matching=SDCM = 5; Standard-=EN 60598-2-3, EN 60598-1 IEC/TR 62778; Standards and approvals=-; Stocking temperature=-; Supply voltage=220 - 240 V; System power=73W; System power :=76 W @ 0.5A; Tilt adjustable=-20° ÷ +10° side bracket - -10° ÷ +20° pole head; Tilt-=-20° ÷ +10° side bracket - -10° ÷ +20° pole head; Type of light source=LED - Not replaceable; Unified Glare Rating=G*3 - ULOR = 0; Unique digital code (Datamatrix)=Currently not present; Voltage-=220/240 V - 50/60 Hz - Bi-power with self-learning; Weight (kg):=8,4; Wiring=Isolating switch
- GWR517430K - ROAD5 MEDI HUGE 4M 3000K 0,7A CL2: Body=Die-cast aluminium -; Catalogue Range=ROAD [5]; Classification:=-; Color Rendering Index=CRI-70; Colore=Graphite grey; Colour :=Powder coating; Colour temperature=3000K; Colour temperature:=3000 K (CRI>80); Context=Street and parking lighting; Control System=Stand alone; DIN 18032-3 certification=-; Descrizione=GWR517430K - ROAD5 MEDI HUGE 4M 3000K 0,7A CL2; Device with reduced surface temperature=-; Driver=Included; Driver Box=Built-in; Efficiency (lm/W)=98; Electrocod=244C; Eletrical and lighting features=-; External screw=Stainless steel; Fixing=Pole Head - Outreach; Gasket=Anti-aging silicone; General information=-; Glow Wire Test :=-; IPEA=ROAD = A // LARGE AREAS = A3 + // CYCLOPEDONALS = A // GREEN AREAS = A // HISTORICAL CENTER = A4 +; Installationa and maintenance=-; LED Life Time (L80B05)=77000H; LED Maintenance=Not available; LED current.=0,7A; Lamp-=LED; Lifetime=L90B10 (Tq+25°C) = 100.000 h - L90B10 (Tq+50°C) = 50.000 h; Locking Hook=Integrated front handle; Lumen output (lm)=10400; Luminaire=LED Road Equipment; Materials=-; Maximum surface exposed to the wind=0,19M2; Maximum surface exposed to the wind :=0.19 m2; Minimum distance from the illuminated object=1M; Modello=GWR517430K; Mouting and installation=Pole Head - Outreach; Nominal flux (lm)=10800; Number of modules=4 (4x3 LED); Operating temperature :=-25 +50 °C; Operating temperature:=-25 +50 °C; Optic=HUGE; Optic :=Metallized polycarbonate reflector; Optic Maintenance=Not available; Optic and illuminating features=-; Overvoltage protection=DM 10KV / CM 10KV; Overvoltage resistance :=Common and dfferential mode: 10KV; Photobiological Risk Class=RG0; Rated frequency (Hz)=50 / 60; SEO=Street lighting; Shield type=4mm thick flat tempered glass; Standard Deviation Colour Matching=SDCM = 5; Standard-=EN 60598-2-3, EN 60598-1 IEC/TR 62778; Standards and approvals=-; Stocking temperature=-; Supply voltage=220 - 240 V; System power=106W; System power :=106 W @ 0.7A; Tilt adjustable=-20° ÷ +10° side bracket - -10° ÷ +20° pole head; Tilt-=-20° ÷ +10° side bracket - -10° ÷ +20° pole head; Tipo alimentatore=Constant Current Driver Led; Tipologia=Stand alone; Type of light source=LED - Not replaceable; Unified Glare Rating=G*3 - ULOR = 0; Unique digital code (Datamatrix)=Currently not present; Voltage-=220/240 V - 50/60 Hz - Stand alone; Weight (kg):=8,4; Wiring=Isolating switch
- GWR5114M - ROAD5 MEDI HUGE 4M 4000K 1,0A CL2 1-10V: Catalogue Range=ROAD [5]; Colour temperature=4000 K (CRI 70); Colour temperature:=4000 K (CRI 70); Descrizione=ROAD 5 DIMM.4M 4000K 1A OPT.ST1; EAN code=8011564858213; Electrocod=244C; LED LifeTime (L80B05)=120000H; LED current.=1A; Lamp-=LED; Lumen output (lm)=13460; Maximum surface exposed to the wind=0,19M2; Minimum distance from the illuminated object=1M; Modello=GWR5114M; No. Chorus modules=4 (4x3 LED); Nominal flux (lm)=19080; Number of modules=4 (4x3 LED); Operating temperature:=-25 +40 °C; Optic=H - ULOR: 0%; Overvoltage resistance=12 KV (Common and dfferential mode); Pilot current=1A; Power supply operation=Dimmable; SEO=Street lighting; System power=113W; Tilt adjustable=-20° ÷ +10° side bracket - -10° ÷ +20° pole head; Tipo alimentatore=Constant Current Driver Led; Tipologia=Dimmable; Voltage-=220/240 V - 50/60 Hz - Dimmable 1-10 V; Weight (kg)=8,4; Weight (kg):=8,4; Working temperature=-25 +40 °C
- GWR517530K - ROAD5 MEDI HUGE 5M 3000K 0,7A CL2: Body=Die-cast aluminium -; Catalogue Range=ROAD [5]; Classification:=-; Color Rendering Index=CRI-70; Colore=Graphite grey; Colour :=Powder coating; Colour temperature=3000K; Colour temperature:=3000 K (CRI>80); Context=Street and parking lighting; Control System=Stand alone; DIN 18032-3 certification=-; Descrizione=GWR517530K - ROAD5 MEDI HUGE 5M 3000K 0,7A CL2; Device with reduced surface temperature=-; Driver=Included; Driver Box=Built-in; Efficiency (lm/W)=98; Electrocod=244C; Eletrical and lighting features=-; External screw=Stainless steel; Fixing=Pole Head - Outreach; Gasket=Anti-aging silicone; General information=-; Glow Wire Test :=-; IPEA=ROAD = B // LARGE AREAS = A ++ // CYCLOPEDONALS = A // GREEN AREAS = A // HISTORICAL CENTER = A4 +; Installationa and maintenance=-; LED Life Time (L80B05)=77000H; LED Maintenance=Not available; LED current.=0,7A; Lamp-=LED; Lifetime=L90B10 (Tq+25°C) = 100.000 h - L90B10 (Tq+50°C) = 50.000 h; Locking Hook=Integrated front handle; Lumen output (lm)=13000; Luminaire=LED Road Equipment; Materials=-; Maximum surface exposed to the wind=0,19M2; Maximum surface exposed to the wind :=0.19 m2; Minimum distance from the illuminated object=1M; Modello=GWR517530K; Mouting and installation=Pole Head - Outreach; Nominal flux (lm)=13500; Number of modules=5 (5x3 LED); Operating temperature :=-25 +50 °C; Operating temperature:=-25 +50 °C; Optic=HUGE; Optic :=Metallized polycarbonate reflector; Optic Maintenance=Not available; Optic and illuminating features=-; Overvoltage protection=DM 10KV / CM 10KV; Overvoltage resistance :=Common and dfferential mode: 10KV; Photobiological Risk Class=RG0; Rated frequency (Hz)=50 / 60; SEO=Street lighting; Shield type=4mm thick flat tempered glass; Standard Deviation Colour Matching=SDCM = 5; Standard-=EN 60598-2-3, EN 60598-1 IEC/TR 62778; Standards and approvals=-; Stocking temperature=-; Supply voltage=220 - 240 V; System power=132W; System power :=132 W @ 0.7A; Tilt adjustable=-20° ÷ +10° side bracket - -10° ÷ +20° pole head; Tilt-=-20° ÷ +10° side bracket - -10° ÷ +20° pole head; Tipo alimentatore=Constant Current Driver Led; Tipologia=Stand alone; Type of light source=LED - Not replaceable; Unified Glare Rating=G*3 - ULOR = 0; Unique digital code (Datamatrix)=Currently not present; Voltage-=220/240 V - 50/60 Hz - Stand alone; Weight (kg):=8,8; Wiring=Isolating switch
- GWR511330K - ROAD5 MEDI HUGE 3M 3000K 1,0A CL2: Body=Die-cast aluminium -; Catalogue Range=ROAD [5]; Classification:=-; Color Rendering Index=CRI-70; Colore=Graphite grey; Colour :=Powder coating; Colour temperature=3000K; Colour temperature:=3000 K (CRI>80); Context=Street and parking lighting; Control System=Stand alone; DIN 18032-3 certification=-; Descrizione=GWR511330K - ROAD5 MEDI HUGE 3M 3000K 1,0A CL2; Device with reduced surface temperature=-; Driver=Included; Driver Box=Built-in; Efficiency (lm/W)=93; Electrocod=244C; Eletrical and lighting features=-; External screw=Stainless steel; Fixing=Pole Head - Outreach; Gasket=Anti-aging silicone; General information=-; Glow Wire Test :=-; IPEA=ROAD = A // LARGE AREAS = A ++ // CYCLOPEDONALS = B // GREEN AREAS = B // HISTORICAL CENTER = A3 +; Installationa and maintenance=-; LED Life Time (L80B05)=120000H; LED Maintenance=Not available; LED current.=1A; Lamp-=LED; Lifetime=L90B10 (Tq+25°C) = 100.000 h - L90B10 (Tq+40°C) = 75.000 h; Locking Hook=Integrated front handle; Lumen output (lm)=10500; Luminaire=LED Road Equipment; Materials=-; Maximum surface exposed to the wind=0,19M2; Maximum surface exposed to the wind :=0.19 m2; Minimum distance from the illuminated object=1M; Modello=GWR511330K; Mouting and installation=Pole Head - Outreach; Nominal flux (lm)=12420; Number of modules=3 (3x3 LED); Operating temperature :=-25 +40 °C; Operating temperature:=-25 +40 °C; Optic=HUGE; Optic :=Metallized polycarbonate reflector; Optic Maintenance=Not available; Optic and illuminating features=-; Overvoltage protection=DM 10KV / CM 10KV; Overvoltage resistance :=Common and dfferential mode: 10KV; Photobiological Risk Class=RG0; Rated frequency (Hz)=50 / 60; SEO=Street lighting; Shield type=4mm thick flat tempered glass; Standard Deviation Colour Matching=SDCM = 5; Standard-=EN 60598-2-3, EN 60598-1 IEC/TR 62778; Standards and approvals=-; Stocking temperature=-; Supply voltage=220 - 240 V; System power=113W; System power :=113 W @ 1A; Tilt adjustable=-20° ÷ +10° side bracket - -10° ÷ +20° pole head; Tilt-=-20° ÷ +10° side bracket - -10° ÷ +20° pole head; Tipo alimentatore=Constant Current Driver Led; Tipologia=Stand alone; Type of light source=LED - Not replaceable; Unified Glare Rating=G*3 - ULOR = 0; Unique digital code (Datamatrix)=Currently not present; Voltage-=220/240 V - 50/60 Hz - Stand alone; Weight (kg):=8; Wiring=Isolating switch
- GWR5115V - ROAD5 MEDI HUGE V 5M 4000K 0,85A CL2: Body=Die-cast aluminium -; Catalogue Range=ROAD [5]; Classification:=-; Color Rendering Index=CRI-70; Colore=Graphite grey; Colour :=Powder coating; Colour temperature=4000K; Colour temperature:=4000 K (CRI>70); Context=Street and parking lighting; Control System=DALI - 5 Step; DIN 18032-3 certification=-; Descrizione=GWR5115V - ROAD5 MEDI HUGE V 5M 4000K 0,85A CL2; Device with reduced surface temperature=-; Driver=Included; Driver Box=Built-in; Efficiency (lm/W)=109; Electrocod=244C; Eletrical and lighting features=-; External screw=Stainless steel; Fixing=Pole Head - Outreach; Gasket=Anti-aging silicone; General information=-; Glow Wire Test :=-; IPEA=ROAD = A + // LARGE AREAS = A4 + // CYCLOPEDONALS = A + // GREEN AREAS = A + // HISTORICAL CENTER = A5 +; Installationa and maintenance=-; LED Life Time (L80B05)=120000H; LED Maintenance=Not available; LED current.=0,849999999999999A; Lamp-=LED; Lifetime=L90B10 (Tq+25°C) = 100.000 h - L90B10 (Tq+40°C) = 50.000 h; Locking Hook=Integrated front handle; Lumen output (lm)=17600; Luminaire=LED Road Equipment; Materials=-; Maximum surface exposed to the wind=0,19M2; Maximum surface exposed to the wind :=0.19 m2; Minimum distance from the illuminated object=1M; Modello=GWR5115V; Mouting and installation=Pole Head - Outreach; Nominal flux (lm)=21230; Number of modules=5 (5x3 LED); Operating temperature :=-25 +40 °C; Operating temperature:=-25 +40 °C; Optic=HUGE; Optic :=Metallized polycarbonate reflector; Optic Maintenance=Not available; Optic and illuminating features=-; Overvoltage protection=DM 10KV / CM 10KV; Photobiological Risk Class=RG0; Rated frequency (Hz)=50 / 60; SEO=Street lighting; Shield type=4mm thick flat tempered glass; Standard Deviation Colour Matching=SDCM = 5; Standard-=EN 60598-2-3, EN 60598-1 IEC/TR 62778; Standards and approvals=-; Stocking temperature=-; Supply voltage=220 - 240 V; System power=159W; System power :=161 W @ 0.85A; Tilt adjustable=-20° ÷ +10° side bracket - -10° ÷ +20° pole head; Tilt-=-20° ÷ +10° side bracket - -10° ÷ +20° pole head; Tipologia=Programmable (5 step); Type of light source=LED - Not replaceable; Unified Glare Rating=G*3 - ULOR = 0; Unique digital code (Datamatrix)=Currently not present; Voltage-=220/240 V - 50/60 Hz - Stand alone and/or programmable; Weight (kg):=8,8; Wiring=Isolating switch
- GWR5114 - ROAD 5 4M 4000K 1A OPT.ST1: Catalogue Range=ROAD [5]; Colour temperature=4000 K (CRI 70); Colour temperature:=4000 K (CRI 70); Descrizione=ROAD 5 4M 4000K 1A OPT.ST1; EAN code=8011564857957; Electrocod=244C; LED LifeTime (L80B05)=120000H; LED current.=1A; Lamp-=LED; Lumen output (lm)=13460; Maximum surface exposed to the wind=0,19M2; Minimum distance from the illuminated object=1M; Modello=GWR5114; No. Chorus modules=4 (4x3 LED); Nominal flux (lm)=19080; Number of modules=4 (4x3 LED); Operating temperature:=-25 +40 °C; Optic=H - ULOR: 0%; Overvoltage resistance=12 KV (Common and dfferential mode); Pilot current=1A; SEO=Street lighting; System power=151W; Tilt adjustable=-20° ÷ +10° side bracket - -10° ÷ +20° pole head; Tipo alimentatore=Constant Current Driver Led; Tipologia=Stand alone; Voltage-=220/240 V - 50/60 Hz - Stand alone; Weight (kg)=8,4; Weight (kg):=8,4; Working temperature=-25 +40 °C
- GWR5176M30K - ROAD5 MEDI HUGE 6M 3000K 0,7A CL2 1-10V: Body=Die-cast aluminium -; Catalogue Range=ROAD [5]; Classification:=-; Color Rendering Index=CRI-70; Colore=Graphite grey; Colour :=Powder coating; Colour temperature=3000K; Colour temperature:=3000 K (CRI>80); Context=Street and parking lighting; Control System=Dimmable 1-10 V; DIN 18032-3 certification=-; Descrizione=GWR5176M30K - ROAD5 MEDI HUGE 6M 3000K 0,7A CL2 1-10V; Device with reduced surface temperature=-; Driver=Included; Driver Box=Built-in; Efficiency (lm/W)=97; Electrocod=244C; Eletrical and lighting features=-; External screw=Stainless steel; Fixing=Pole Head - Outreach; Gasket=Anti-aging silicone; General information=-; Glow Wire Test :=-; IPEA=ROAD = B // LARGE AREAS = A ++ // CYCLOPEDONALS = A // GREEN AREAS = A // HISTORICAL CENTER = A3 +; Installationa and maintenance=-; LED Life Time (L80B05)=77000H; LED Maintenance=Not available; LED current.=0,7A; Lamp-=LED; Lifetime=L90B10 (Tq+25°C) = 100.000 h - L90B10 (Tq+50°C) = 50.000 h; Locking Hook=Integrated front handle; Lumen output (lm)=15600; Luminaire=LED Road Equipment; Materials=-; Maximum surface exposed to the wind=0,19M2; Maximum surface exposed to the wind :=0.19 m2; Minimum distance from the illuminated object=1M; Modello=GWR5176M30K; Mouting and installation=Pole Head - Outreach; Nominal flux (lm)=16200; Number of modules=6 (6x3 LED); Operating temperature :=-25 +50 °C; Operating temperature:=-25 +50 °C; Optic=HUGE; Optic :=Metallized polycarbonate reflector; Optic Maintenance=Not available; Optic and illuminating features=-; Overvoltage protection=DM 10KV / CM 10KV; Overvoltage resistance :=Common and dfferential mode: 10KV; Photobiological Risk Class=RG0; Power supply operation=Dimmable; Rated frequency (Hz)=50 / 60; SEO=Street lighting; Shield type=4mm thick flat tempered glass; Standard Deviation Colour Matching=SDCM = 5; Standard-=EN 60598-2-3, EN 60598-1 IEC/TR 62778; Standards and approvals=-; Stocking temperature=-; Supply voltage=220 - 240 V; System power=159W; System power :=161 W @ 0.7A; Tilt adjustable=-20° ÷ +10° side bracket - -10° ÷ +20° pole head; Tilt-=-20° ÷ +10° side bracket - -10° ÷ +20° pole head; Tipo alimentatore=Constant Current Driver Led; Tipologia=Dimmable; Type of light source=LED - Not replaceable; Unified Glare Rating=G*3 - ULOR = 0; Unique digital code (Datamatrix)=Currently not present; Voltage-=220/240 V - 50/60 Hz - Dimmable 1-10 V; Weight (kg):=9,09999999999999; Wiring=Isolating switch
- GWR517330K - ROAD5 MEDI HUGE 3M 3000K 0,7A CL2: Body=Die-cast aluminium -; Catalogue Range=ROAD [5]; Classification:=-; Color Rendering Index=CRI-70; Colore=Graphite grey; Colour :=Powder coating; Colour temperature=3000K; Colour temperature:=3000 K (CRI>80); Context=Street and parking lighting; Control System=Stand alone; DIN 18032-3 certification=-; Descrizione=GWR517330K - ROAD5 MEDI HUGE 3M 3000K 0,7A CL2; Device with reduced surface temperature=-; Driver=Included; Driver Box=Built-in; Efficiency (lm/W)=99; Electrocod=244C; Eletrical and lighting features=-; External screw=Stainless steel; Fixing=Pole Head - Outreach; Gasket=Anti-aging silicone; General information=-; Glow Wire Test :=-; IPEA=ROAD = A ++ // LARGE AREAS = A3 + // CYCLOPEDONALS = A + // GREEN AREAS = A + // HISTORICAL CENTER = A5 +; Installationa and maintenance=-; LED Life Time (L80B05)=77000H; LED Maintenance=Not available; LED current.=0,7A; Lamp-=LED; Lifetime=L90B10 (Tq+25°C) = 100.000 h - L90B10 (Tq+50°C) = 75.000 h; Locking Hook=Integrated front handle; Lumen output (lm)=7800; Luminaire=LED Road Equipment; Materials=-; Maximum surface exposed to the wind=0,19M2; Maximum surface exposed to the wind :=0.19 m2; Minimum distance from the illuminated object=1M; Modello=GWR517330K; Mouting and installation=Pole Head - Outreach; Nominal flux (lm)=8100; Number of modules=3 (3x3 LED); Operating temperature :=-25 +50 °C; Operating temperature:=-25 +50 °C; Optic=HUGE; Optic :=Metallized polycarbonate reflector; Optic Maintenance=Not available; Optic and illuminating features=-; Overvoltage protection=DM 10KV / CM 10KV; Overvoltage resistance :=Common and dfferential mode: 10KV; Photobiological Risk Class=RG0; Rated frequency (Hz)=50 / 60; SEO=Street lighting; Shield type=4mm thick flat tempered glass; Standard Deviation Colour Matching=SDCM = 5; Standard-=EN 60598-2-3, EN 60598-1 IEC/TR 62778; Standards and approvals=-; Stocking temperature=-; Supply voltage=220 - 240 V; System power=79W; System power :=79 W @ 0.7A; Tilt adjustable=-20° ÷ +10° side bracket - -10° ÷ +20° pole head; Tilt-=-20° ÷ +10° side bracket - -10° ÷ +20° pole head; Tipo alimentatore=Constant Current Driver Led; Tipologia=Stand alone; Type of light source=LED - Not replaceable; Unified Glare Rating=G*3 - ULOR = 0; Unique digital code (Datamatrix)=Currently not present; Voltage-=220/240 V - 50/60 Hz - Stand alone; Weight (kg):=8; Wiring=Isolating switch
- GWR5173 - ROAD 5 3M 4000K 700mA OPT.ST1: Catalogue Range=ROAD [5]; Colour temperature=4000 K (CRI 70); Colour temperature:=4000 K (CRI 70); Descrizione=ROAD 5 3M 4000K 700mA OPT.ST1; EAN code=8011564857926; Electrocod=244C; LED LifeTime (L80B05)=77000H; LED current.=0,7A; Lamp-=LED; Lumen output (lm)=6890; Maximum surface exposed to the wind=0,19M2; Minimum distance from the illuminated object=1M; Modello=GWR5173; No. Chorus modules=3 (3x3 LED); Nominal flux (lm)=9360; Number of modules=3 (3x3 LED); Operating temperature:=-25 +50 °C; Optic=H - ULOR: 0%; Overvoltage resistance=12 KV (Common and dfferential mode); Pilot current=0,7A; SEO=Street lighting; System power=79W; Tilt adjustable=-20° ÷ +10° side bracket - -10° ÷ +20° pole head; Tipo alimentatore=Constant Current Driver Led; Tipologia=Stand alone; Voltage-=220/240 V - 50/60 Hz - Stand alone; Weight (kg)=8; Weight (kg):=8; Working temperature=-25 +50 °C
- GWR5155M - ROAD5 MEDI HUGE 5M 4000K 0,5A CL2 1-10V: Body=Die-cast aluminium -; Catalogue Range=ROAD [5]; Classification:=-; Color Rendering Index=CRI-70; Colore=Graphite grey; Colour :=Powder coating; Colour temperature=4000K; Colour temperature:=4000 K (CRI>70); Context=Street and parking lighting; Control System=Dimmable 1-10 V; DIN 18032-3 certification=-; Descrizione=GWR5155M - ROAD5 MEDI HUGE 5M 4000K 0,5A CL2 1-10V; Device with reduced surface temperature=-; Driver=Included; Driver Box=Built-in; Efficiency (lm/W)=117; Electrocod=244C; Eletrical and lighting features=-; External screw=Stainless steel; Fixing=Pole Head - Outreach; Gasket=Anti-aging silicone; General information=-; Glow Wire Test :=-; IPEA=ROAD = A3 + // LARGE AREAS = A5 + // CYCLOPEDONALS = A ++ // GREEN AREAS = A ++ // HISTORICAL CENTER = A6 +; Installationa and maintenance=-; LED Life Time (L80B05)=120000H; LED Maintenance=Not available; LED current.=0,5A; Lamp-=LED; Lifetime=L90B10 (Tq+25°C) = 100.000 h - L90B10 (Tq+50°C) = 50.000 h; Locking Hook=Integrated front handle; Lumen output (lm)=11000; Luminaire=LED Road Equipment; Materials=-; Maximum surface exposed to the wind=0,19M2; Maximum surface exposed to the wind :=0.19 m2; Minimum distance from the illuminated object=1M; Modello=GWR5155M; Mouting and installation=Pole Head - Outreach; Nominal flux (lm)=12000; Number of modules=5 (5x3 LED); Operating temperature :=-25 +50 °C; Operating temperature:=-25 +40 °C; Optic=HUGE; Optic :=Metallized polycarbonate reflector; Optic Maintenance=Not available; Optic and illuminating features=-; Overvoltage protection=DM 10KV / CM 10KV; Photobiological Risk Class=RG0; Rated frequency (Hz)=50 / 60; SEO=Street lighting; Shield type=4mm thick flat tempered glass; Standard Deviation Colour Matching=SDCM = 5; Standard-=EN 60598-2-3, EN 60598-1 IEC/TR 62778; Standards and approvals=-; Stocking temperature=-; Supply voltage=220 - 240 V; System power=91W; System power :=94 W @ 0.5A; Tilt adjustable=-20° ÷ +10° side bracket - -10° ÷ +20° pole head; Tilt-=-20° ÷ +10° side bracket - -10° ÷ +20° pole head; Tipologia=Dimmable; Type of light source=LED - Not replaceable; Unified Glare Rating=G*3 - ULOR = 0; Unique digital code (Datamatrix)=Currently not present; Voltage-=220/240 V - 50/60 Hz - Dimmable 1-10 V; Weight (kg):=8,8; Wiring=Isolating switch
- GWR5116M - ROAD5 MEDI HUGE 6M 4000K 0,85A CL2 1-10V: Catalogue Range=ROAD [5]; Colour temperature=4000 K (CRI 70); Colour temperature:=4000 K (CRI 70); Descrizione=ROAD 5 DIMM.6M 4000K 0,85A OPT.ST1; EAN code=8011564858251; Electrocod=244C; LED LifeTime (L80B05)=120000H; LED current.=0,85A; Lamp-=LED; Lumen output (lm)=17160; Maximum surface exposed to the wind=0,19M2; Minimum distance from the illuminated object=1M; Modello=GWR5116M; No. Chorus modules=6 (6x3 LED); Nominal flux (lm)=24330; Number of modules=6 (6x3 LED); Operating temperature:=-25 +40 °C; Optic=H - ULOR: 0%; Overvoltage resistance=12 KV (Common and dfferential mode); Pilot current=0,85A; Power supply operation=Dimmable; SEO=Street lighting; System power=185W; Tilt adjustable=-20° ÷ +10° side bracket - -10° ÷ +20° pole head; Tipo alimentatore=Constant Current Driver Led; Tipologia=Dimmable; Voltage-=220/240 V - 50/60 Hz - Dimmable 1-10 V; Weight (kg)=9.1; Weight (kg):=9,1; Working temperature=-25 +40 °C
- GWR5114B30K - ROAD5 MEDI HUGE 4M 3000K 1,0A CL2 BIREG: Body=Die-cast aluminium -; Catalogue Range=ROAD [5]; Classification:=-; Color Rendering Index=CRI-70; Colore=Graphite grey; Colour :=Powder coating; Colour temperature=3000K; Colour temperature:=3000 K (CRI>80); Context=Street and parking lighting; Control System=Bi-power with self-learning; DIN 18032-3 certification=-; Descrizione=GWR5114B30K - ROAD5 MEDI HUGE 4M 3000K 1,0A CL2 BIREG; Device with reduced surface temperature=-; Driver=Included; Driver Box=Built-in; Efficiency (lm/W)=92; Electrocod=244C; Eletrical and lighting features=-; External screw=Stainless steel; Fixing=Pole Head - Outreach; Gasket=Anti-aging silicone; General information=-; Glow Wire Test :=-; IPEA=ROAD = B // LARGE AREAS = A + // CYCLOPEDONALS = B // GREEN AREAS = B // HISTORICAL CENTER = A3 +; Installationa and maintenance=-; LED Life Time (L80B05)=120000H; LED Maintenance=Not available; LED current.=1A; Lamp-=LED; Lifetime=L90B10 (Tq+25°C) = 100.000 h - L90B10 (Tq+40°C) = 50.000 h; Locking Hook=Integrated front handle; Lumen output (lm)=14000; Luminaire=LED Road Equipment; Materials=-; Maximum surface exposed to the wind=0,19M2; Maximum surface exposed to the wind :=0.19 m2; Minimum distance from the illuminated object=1M; Modello=GWR5114B30K; Mouting and installation=Pole Head - Outreach; Nominal flux (lm)=16560; Number of modules=4 (4x3 LED); Operating temperature :=-25 +40 °C; Operating temperature:=-25 +40 °C; Optic=HUGE; Optic :=Metallized polycarbonate reflector; Optic Maintenance=Not available; Optic and illuminating features=-; Overvoltage protection=DM 10KV / CM 10KV; Overvoltage resistance :=Common and dfferential mode: 10KV; Photobiological Risk Class=RG0; Power supply operation=Bi power; Rated frequency (Hz)=50 / 60; SEO=Street lighting; Shield type=4mm thick flat tempered glass; Standard Deviation Colour Matching=SDCM = 5; Standard-=EN 60598-2-3, EN 60598-1 IEC/TR 62778; Standards and approvals=-; Stocking temperature=-; Supply voltage=220 - 240 V; System power=153W; System power :=153 W @ 1A; Tilt adjustable=-20° ÷ +10° side bracket - -10° ÷ +20° pole head; Tilt-=-20° ÷ +10° side bracket - -10° ÷ +20° pole head; Tipo alimentatore=Constant Current Driver Led; Tipologia=Bi power; Type of light source=LED - Not replaceable; Unified Glare Rating=G*3 - ULOR = 0; Unique digital code (Datamatrix)=Currently not present; Voltage-=220/240 V - 50/60 Hz - Bi-power with self-learning; Weight (kg):=8,4; Wiring=Isolating switch
- GWR5114D - ROAD5 MEDI HUGE 4M 4000K 1A CL2 DALI: Body=Die-cast aluminium -; Classification:=-; Color Rendering Index=CRI-70; Colore=Graphite grey; Colour :=Powder coating; Colour temperature=4000K; Context=Street and parking lighting; Control System=DALI; DIN 18032-3 certification=-; Descrizione=GWR5114D - ROAD5 MEDI HUGE 4M 4000K 1A CL2 DALI; Device with reduced surface temperature=-; Driver=Included; Driver Box=Built-in; Efficiency (lm/W)=105; Eletrical and lighting features=-; External screw=Stainless steel; Fixing=Pole Head - Outreach; Gasket=Anti-aging silicone; General information=-; Glow Wire Test :=-; IPEA=ROAD = A // LARGE AREAS = A3 + // CYCLOPEDONALS = A // GREEN AREAS = A // HISTORICAL CENTER = A5 +; Installationa and maintenance=-; LED Maintenance=Not available; Lifetime=L90B10 (Tq+25°C) = 100.000 h - L90B10 (Tq+40°C) = 50.000 h; Locking Hook=Integrated front handle; Lumen output (lm)=16100; Luminaire=LED Road Equipment; Materials=-; Maximum surface exposed to the wind :=0.19 m2; Modello=GWR5114D; Mouting and installation=Pole Head - Outreach; Number of modules=4 (4x3 LED); Operating temperature :=-25 +40 °C; Optic=HUGE; Optic :=Metallized polycarbonate reflector; Optic Maintenance=Not available; Optic and illuminating features=-; Overvoltage protection=DM 10KV / CM 10KV; Photobiological Risk Class=RG0; Rated frequency (Hz)=50 / 60; Shield type=4mm thick flat tempered glass; Standard Deviation Colour Matching=SDCM = 5; Standard-=EN 60598-2-3, EN 60598-1 IEC/TR 62778; Standards and approvals=-; Stocking temperature=-; Supply voltage=220 - 240 V; System power :=153 W @ 1A; Tilt-=-20° ÷ +10° side bracket - -10° ÷ +20° pole head; Type of light source=LED - Not replaceable; Unified Glare Rating=G*3 - ULOR = 0; Unique digital code (Datamatrix)=Currently not present; Weight (kg):=8,4; Wiring=Isolating switch
- GWR5173B - ROAD5 MEDI HUGE 3M 4000K 0,7A CL2 BIREG: Catalogue Range=ROAD [5]; Colour temperature=4000 K (CRI 70); Colour temperature:=4000 K (CRI 70); Descrizione=ROAD 5 BI-POW.3M 4000K 700mA OPT.ST1; EAN code=8011564858008; Electrocod=244C; LED LifeTime (L80B05)=77000H; LED current.=0,7A; Lamp-=LED; Lumen output (lm)=6890; Maximum surface exposed to the wind=0,19M2; Minimum distance from the illuminated object=1M; Modello=GWR5173B; No. Chorus modules=3 (3x3 LED); Nominal flux (lm)=9360; Number of modules=3 (3x3 LED); Operating temperature:=-25 +50 °C; Optic=H - ULOR: 0%; Overvoltage resistance=12 KV (Common and dfferential mode); Pilot current=0,7A; Power supply operation=Bi power; SEO=Street lighting; System power=81W; Tilt adjustable=-20° ÷ +10° side bracket - -10° ÷ +20° pole head; Tipo alimentatore=Constant Current Driver Led; Tipologia=Bi power; Voltage-=220/240 V - 50/60 Hz - Bi-power with self-learning; Weight (kg)=8; Weight (kg):=8; Working temperature=-25 +50 °C
- GWR5175M30K - ROAD5 MEDI HUGE 5M 3000K 0,7A CL2 1-10V: Body=Die-cast aluminium -; Catalogue Range=ROAD [5]; Classification:=-; Color Rendering Index=CRI-70; Colore=Graphite grey; Colour :=Powder coating; Colour temperature=3000K; Colour temperature:=3000 K (CRI>80); Context=Street and parking lighting; Control System=Dimmable 1-10 V; DIN 18032-3 certification=-; Descrizione=GWR5175M30K - ROAD5 MEDI HUGE 5M 3000K 0,7A CL2 1-10V; Device with reduced surface temperature=-; Driver=Included; Driver Box=Built-in; Efficiency (lm/W)=97; Electrocod=244C; Eletrical and lighting features=-; External screw=Stainless steel; Fixing=Pole Head - Outreach; Gasket=Anti-aging silicone; General information=-; Glow Wire Test :=-; IPEA=ROAD = B // LARGE AREAS = A ++ // CYCLOPEDONALS = A // GREEN AREAS = A // HISTORICAL CENTER = A3 +; Installationa and maintenance=-; LED Life Time (L80B05)=77000H; LED Maintenance=Not available; LED current.=0,7A; Lamp-=LED; Lifetime=L90B10 (Tq+25°C) = 100.000 h - L90B10 (Tq+50°C) = 50.000 h; Locking Hook=Integrated front handle; Lumen output (lm)=13000; Luminaire=LED Road Equipment; Materials=-; Maximum surface exposed to the wind=0,19M2; Maximum surface exposed to the wind :=0.19 m2; Minimum distance from the illuminated object=1M; Modello=GWR5175M30K; Mouting and installation=Pole Head - Outreach; Nominal flux (lm)=13500; Number of modules=5 (5x3 LED); Operating temperature :=-25 +50 °C; Operating temperature:=-25 +50 °C; Optic=HUGE; Optic :=Metallized polycarbonate reflector; Optic Maintenance=Not available; Optic and illuminating features=-; Overvoltage protection=DM 10KV / CM 10KV; Overvoltage resistance :=Common and dfferential mode: 10KV; Photobiological Risk Class=RG0; Power supply operation=Dimmable; Rated frequency (Hz)=50 / 60; SEO=Street lighting; Shield type=4mm thick flat tempered glass; Standard Deviation Colour Matching=SDCM = 5; Standard-=EN 60598-2-3, EN 60598-1 IEC/TR 62778; Standards and approvals=-; Stocking temperature=-; Supply voltage=220 - 240 V; System power=132W; System power :=134 W @ 0.7A; Tilt adjustable=-20° ÷ +10° side bracket - -10° ÷ +20° pole head; Tilt-=-20° ÷ +10° side bracket - -10° ÷ +20° pole head; Tipo alimentatore=Constant Current Driver Led; Tipologia=Dimmable; Type of light source=LED - Not replaceable; Unified Glare Rating=G*3 - ULOR = 0; Unique digital code (Datamatrix)=Currently not present; Voltage-=220/240 V - 50/60 Hz - Dimmable 1-10 V; Weight (kg):=8,8; Wiring=Isolating switch
- GWR5114M30K - ROAD5 MEDI HUGE 4M 3000K 1,0A CL2 1-10V: Body=Die-cast aluminium -; Catalogue Range=ROAD [5]; Classification:=-; Color Rendering Index=CRI-70; Colore=Graphite grey; Colour :=Powder coating; Colour temperature=3000K; Colour temperature:=3000 K (CRI>80); Context=Street and parking lighting; Control System=Dimmable 1-10 V; DIN 18032-3 certification=-; Descrizione=GWR5114M30K - ROAD5 MEDI HUGE 4M 3000K 1,0A CL2 1-10V; Device with reduced surface temperature=-; Driver=Included; Driver Box=Built-in; Efficiency (lm/W)=92; Electrocod=244C; Eletrical and lighting features=-; External screw=Stainless steel; Fixing=Pole Head - Outreach; Gasket=Anti-aging silicone; General information=-; Glow Wire Test :=-; IPEA=ROAD = B // LARGE AREAS = A + // CYCLOPEDONALS = B // GREEN AREAS = B // HISTORICAL CENTER = A3 +; Installationa and maintenance=-; LED Life Time (L80B05)=120000H; LED Maintenance=Not available; LED current.=1A; Lamp-=LED; Lifetime=L90B10 (Tq+25°C) = 100.000 h - L90B10 (Tq+40°C) = 50.000 h; Locking Hook=Integrated front handle; Lumen output (lm)=14000; Luminaire=LED Road Equipment; Materials=-; Maximum surface exposed to the wind=0,19M2; Maximum surface exposed to the wind :=0.19 m2; Minimum distance from the illuminated object=1M; Modello=GWR5114M30K; Mouting and installation=Pole Head - Outreach; Nominal flux (lm)=16560; Number of modules=4 (4x3 LED); Operating temperature :=-25 +40 °C; Operating temperature:=-25 +40 °C; Optic=HUGE; Optic :=Metallized polycarbonate reflector; Optic Maintenance=Not available; Optic and illuminating features=-; Overvoltage protection=DM 10KV / CM 10KV; Overvoltage resistance :=Common and dfferential mode: 10KV; Photobiological Risk Class=RG0; Power supply operation=Dimmable; Rated frequency (Hz)=50 / 60; SEO=Street lighting; Shield type=4mm thick flat tempered glass; Standard Deviation Colour Matching=SDCM = 5; Standard-=EN 60598-2-3, EN 60598-1 IEC/TR 62778; Standards and approvals=-; Stocking temperature=-; Supply voltage=220 - 240 V; System power=113W; System power :=153 W @ 1A; Tilt adjustable=-20° ÷ +10° side bracket - -10° ÷ +20° pole head; Tilt-=-20° ÷ +10° side bracket - -10° ÷ +20° pole head; Tipo alimentatore=Constant Current Driver Led; Tipologia=Dimmable; Type of light source=LED - Not replaceable; Unified Glare Rating=G*3 - ULOR = 0; Unique digital code (Datamatrix)=Currently not present; Voltage-=220/240 V - 50/60 Hz - Dimmable 1-10 V; Weight (kg):=8,4; Wiring=Isolating switch
- GWR5113M - ROAD5 MEDI HUGE 3M 4000K 1,0A CL2 1-10V: Catalogue Range=ROAD [5]; Colour temperature=4000 K (CRI 70); Colour temperature:=4000 K (CRI 70); Descrizione=ROAD 5 DIMM.3M 4000K 1A OPT.ST1; EAN code=8011564858091; Electrocod=244C; LED LifeTime (L80B05)=120000H; LED current.=1A; Lamp-=LED; Lumen output (lm)=10100; Maximum surface exposed to the wind=0,19M2; Minimum distance from the illuminated object=1M; Modello=GWR5113M; No. Chorus modules=3 (3x3 LED); Nominal flux (lm)=14310; Number of modules=3 (3x3 LED); Operating temperature:=-25 +40 °C; Optic=H - ULOR: 0%; Overvoltage resistance=12 KV (Common and dfferential mode); Pilot current=1A; Power supply operation=Dimmable; SEO=Street lighting; System power=113W; Tilt adjustable=-20° ÷ +10° side bracket - -10° ÷ +20° pole head; Tipo alimentatore=Constant Current Driver Led; Tipologia=Dimmable; Voltage-=220/240 V - 50/60 Hz - Dimmable 1-10 V; Weight (kg)=8; Weight (kg):=8; Working temperature=-25 +40 °C
- GWR5113B - ROAD 5 BI-POW.3M 4000K 1A OPT.ST1: Catalogue Range=ROAD [5]; Colour temperature=4000 K (CRI 70); Colour temperature:=4000 K (CRI 70); Descrizione=ROAD 5 BI-POW.3M 4000K 1A OPT.ST1; EAN code=8011564858015; Electrocod=244C; LED LifeTime (L80B05)=120000H; LED current.=1A; Lamp-=LED; Lumen output (lm)=10100; Maximum surface exposed to the wind=0,19M2; Minimum distance from the illuminated object=1M; Modello=GWR5113B; No. Chorus modules=3 (3x3 LED); Nominal flux (lm)=14310; Number of modules=3 (3x3 LED); Operating temperature:=-25 +40 °C; Optic=H - ULOR: 0%; Overvoltage resistance=12 KV (Common and dfferential mode); Pilot current=1A; Power supply operation=Bi power; SEO=Street lighting; System power=115W; Tilt adjustable=-20° ÷ +10° side bracket - -10° ÷ +20° pole head; Tipo alimentatore=Constant Current Driver Led; Tipologia=Bi power; Voltage-=220/240 V - 50/60 Hz - Bi-power with self-learning; Weight (kg)=8; Weight (kg):=8; Working temperature=-25 +40 °C
- GWR5115B - ROAD 5 BI-POW.5M 4000K 0,85A OPT.ST1: Catalogue Range=ROAD [5]; Colour temperature=4000 K (CRI 70); Colour temperature:=4000 K (CRI 70); Descrizione=ROAD 5 BI-POW.5M 4000K 0,85A OPT.ST1; EAN code=8011564858053; Electrocod=244C; LED LifeTime (L80B05)=120000H; LED current.=0,85A; Lamp-=LED; Lumen output (lm)=14970; Maximum surface exposed to the wind=0,19M2; Minimum distance from the illuminated object=1M; Modello=GWR5115B; No. Chorus modules=5 (5x3 LED); Nominal flux (lm)=21230; Number of modules=5 (5x3 LED); Operating temperature:=-25 +40 °C; Optic=H - ULOR: 0%; Overvoltage resistance=12 KV (Common and dfferential mode); Pilot current=0,85A; Power supply operation=Bi power; SEO=Street lighting; System power=161W; Tilt adjustable=-20° ÷ +10° side bracket - -10° ÷ +20° pole head; Tipo alimentatore=Constant Current Driver Led; Tipologia=Bi power; Voltage-=220/240 V - 50/60 Hz - Bi-power with self-learning; Weight (kg)=8,8; Weight (kg):=8,8; Working temperature=-25 +40 °C
- GWR5153M - ROAD5 MEDI HUGE 3M 4000K 0,5A CL2 1-10V: Body=Die-cast aluminium -; Catalogue Range=ROAD [5]; Classification:=-; Color Rendering Index=CRI-70; Colore=Graphite grey; Colour :=Powder coating; Colour temperature=4000K; Colour temperature:=4000 K (CRI>70); Context=Street and parking lighting; Control System=Dimmable 1-10 V; DIN 18032-3 certification=-; Descrizione=GWR5153M - ROAD5 MEDI HUGE 3M 4000K 0,5A CL2 1-10V; Device with reduced surface temperature=-; Driver=Included; Driver Box=Built-in; Efficiency (lm/W)=114; Electrocod=244C; Eletrical and lighting features=-; External screw=Stainless steel; Fixing=Pole Head - Outreach; Gasket=Anti-aging silicone; General information=-; Glow Wire Test :=-; IPEA=ROAD = A4 + // LARGE AREAS = A5 + // CYCLOPEDONALS = A4 + // GREEN AREAS = A4 + // HISTORICAL CENTER = A6 +; Installationa and maintenance=-; LED Life Time (L80B05)=120000H; LED Maintenance=Not available; LED current.=0,5A; Lamp-=LED; Lifetime=L90B10 (Tq+25°C) = 100.000 h - L90B10 (Tq+50°C) = 75.000 h; Locking Hook=Integrated front handle; Lumen output (lm)=6600; Luminaire=LED Road Equipment; Materials=-; Maximum surface exposed to the wind=0,19M2; Maximum surface exposed to the wind :=0.19 m2; Minimum distance from the illuminated object=1M; Modello=GWR5153M; Mouting and installation=Pole Head - Outreach; Nominal flux (lm)=7200; Number of modules=3 (3x3 LED); Operating temperature :=-25 +50 °C; Operating temperature:=-25 +40 °C; Optic=HUGE; Optic :=Metallized polycarbonate reflector; Optic Maintenance=Not available; Optic and illuminating features=-; Overvoltage protection=DM 10KV / CM 10KV; Photobiological Risk Class=RG0; Rated frequency (Hz)=50 / 60; SEO=Street lighting; Shield type=4mm thick flat tempered glass; Standard Deviation Colour Matching=SDCM = 5; Standard-=EN 60598-2-3, EN 60598-1 IEC/TR 62778; Standards and approvals=-; Stocking temperature=-; Supply voltage=220 - 240 V; System power=54W; System power :=58 W @ 0.5A; Tilt adjustable=-20° ÷ +10° side bracket - -10° ÷ +20° pole head; Tilt-=-20° ÷ +10° side bracket - -10° ÷ +20° pole head; Tipologia=Dimmable; Type of light source=LED - Not replaceable; Unified Glare Rating=G*3 - ULOR = 0; Unique digital code (Datamatrix)=Currently not present; Voltage-=220/240 V - 50/60 Hz - Dimmable 1-10 V; Weight (kg):=8; Wiring=Isolating switch
- GWR5174V - ROAD5 MEDI HUGE V 4M 4000K 0,7A CL2: Body=Die-cast aluminium -; Catalogue Range=ROAD [5]; Classification:=-; Color Rendering Index=CRI-70; Colore=Graphite grey; Colour :=Powder coating; Colour temperature=4000K; Colour temperature:=4000 K (CRI>70); Context=Street and parking lighting; Control System=DALI - 5 Step; DIN 18032-3 certification=-; Descrizione=GWR5174V - ROAD5 MEDI HUGE V 4M 4000K 0,7A CL2; Device with reduced surface temperature=-; Driver=Included; Driver Box=Built-in; Efficiency (lm/W)=111; Electrocod=244C; Eletrical and lighting features=-; External screw=Stainless steel; Fixing=Pole Head - Outreach; Gasket=Anti-aging silicone; General information=-; Glow Wire Test :=-; IPEA=ROAD = A ++ // LARGE AREAS = A4 + // CYCLOPEDONALS = A ++ // GREEN AREAS = A ++ // HISTORICAL CENTER = A6 +; Installationa and maintenance=-; LED Life Time (L80B05)=120000H; LED Maintenance=Not available; LED current.=0,7A; Lamp-=LED; Lifetime=L90B10 (Tq+25°C) = 100.000 h - L90B10 (Tq+50°C) = 50.000 h; Locking Hook=Integrated front handle; Lumen output (lm)=12000; Luminaire=LED Road Equipment; Materials=-; Maximum surface exposed to the wind=0,19M2; Maximum surface exposed to the wind :=0.19 m2; Minimum distance from the illuminated object=1M; Modello=GWR5174V; Mouting and installation=Pole Head - Outreach; Nominal flux (lm)=12480; Number of modules=4 (4x3 LED); Operating temperature :=-25 +50 °C; Operating temperature:=-25 +40 °C; Optic=HUGE; Optic :=Metallized polycarbonate reflector; Optic Maintenance=Not available; Optic and illuminating features=-; Overvoltage protection=DM 10KV / CM 10KV; Photobiological Risk Class=RG0; Rated frequency (Hz)=50 / 60; SEO=Street lighting; Shield type=4mm thick flat tempered glass; Standard Deviation Colour Matching=SDCM = 5; Standard-=EN 60598-2-3, EN 60598-1 IEC/TR 62778; Standards and approvals=-; Stocking temperature=-; Supply voltage=220 - 240 V; System power=106W; System power :=108 W @ 0.7A; Tilt adjustable=-20° ÷ +10° side bracket - -10° ÷ +20° pole head; Tilt-=-20° ÷ +10° side bracket - -10° ÷ +20° pole head; Tipologia=Programmable (5 step); Type of light source=LED - Not replaceable; Unified Glare Rating=G*3 - ULOR = 0; Unique digital code (Datamatrix)=Currently not present; Voltage-=220/240 V - 50/60 Hz - Stand alone and/or programmable; Weight (kg):=8,4; Wiring=Isolating switch
- GWR5113M30K - ROAD5 MEDI HUGE 3M 3000K 1,0A CL2 1-10V: Body=Die-cast aluminium -; Catalogue Range=ROAD [5]; Classification:=-; Color Rendering Index=CRI-70; Colore=Graphite grey; Colour :=Powder coating; Colour temperature=3000K; Colour temperature:=3000 K (CRI>80); Context=Street and parking lighting; Control System=Dimmable 1-10 V; DIN 18032-3 certification=-; Descrizione=GWR5113M30K - ROAD5 MEDI HUGE 3M 3000K 1,0A CL2 1-10V; Device with reduced surface temperature=-; Driver=Included; Driver Box=Built-in; Efficiency (lm/W)=91; Electrocod=244C; Eletrical and lighting features=-; External screw=Stainless steel; Fixing=Pole Head - Outreach; Gasket=Anti-aging silicone; General information=-; Glow Wire Test :=-; IPEA=ROAD = A // LARGE AREAS = A ++ // CYCLOPEDONALS = B // GREEN AREAS = B // HISTORICAL CENTER = A3 +; Installationa and maintenance=-; LED Life Time (L80B05)=120000H; LED Maintenance=Not available; LED current.=1A; Lamp-=LED; Lifetime=L90B10 (Tq+25°C) = 100.000 h - L90B10 (Tq+40°C) = 75.000 h; Locking Hook=Integrated front handle; Lumen output (lm)=10500; Luminaire=LED Road Equipment; Materials=-; Maximum surface exposed to the wind=0,19M2; Maximum surface exposed to the wind :=0.19 m2; Minimum distance from the illuminated object=1M; Modello=GWR5113M30K; Mouting and installation=Pole Head - Outreach; Nominal flux (lm)=12420; Number of modules=3 (3x3 LED); Operating temperature :=-25 +40 °C; Operating temperature:=-25 +40 °C; Optic=HUGE; Optic :=Metallized polycarbonate reflector; Optic Maintenance=Not available; Optic and illuminating features=-; Overvoltage protection=DM 10KV / CM 10KV; Overvoltage resistance :=Common and dfferential mode: 10KV; Photobiological Risk Class=RG0; Power supply operation=Dimmable; Rated frequency (Hz)=50 / 60; SEO=Street lighting; Shield type=4mm thick flat tempered glass; Standard Deviation Colour Matching=SDCM = 5; Standard-=EN 60598-2-3, EN 60598-1 IEC/TR 62778; Standards and approvals=-; Stocking temperature=-; Supply voltage=220 - 240 V; System power=113W; System power :=115 W @ 1A; Tilt adjustable=-20° ÷ +10° side bracket - -10° ÷ +20° pole head; Tilt-=-20° ÷ +10° side bracket - -10° ÷ +20° pole head; Tipo alimentatore=Constant Current Driver Led; Tipologia=Dimmable; Type of light source=LED - Not replaceable; Unified Glare Rating=G*3 - ULOR = 0; Unique digital code (Datamatrix)=Currently not present; Voltage-=220/240 V - 50/60 Hz - Dimmable 1-10 V; Weight (kg):=8; Wiring=Isolating switch
- GWR5176 - ROAD5 MEDI HUGE 6M 4000K 0,7A CL2: Catalogue Range=ROAD [5]; Colour temperature=4000 K (CRI 70); Colour temperature:=4000 K (CRI 70); Descrizione=ROAD 5 6M 4000K 700mA OPT.ST1; EAN code=8011564857988; Electrocod=244C; LED LifeTime (L80B05)=77000H; LED current.=0,7A; Lamp-=LED; Lumen output (lm)=13780; Maximum surface exposed to the wind=0,19M2; Minimum distance from the illuminated object=1M; Modello=GWR5176; No. Chorus modules=6 (6x3 LED); Nominal flux (lm)=18720; Number of modules=6 (6x3 LED); Operating temperature:=-25 +50 °C; Optic=H - ULOR: 0%; Overvoltage resistance=12 KV (Common and dfferential mode); Pilot current=0,7A; SEO=Street lighting; System power=159W; Tilt adjustable=-20° ÷ +10° side bracket - -10° ÷ +20° pole head; Tipo alimentatore=Constant Current Driver Led; Tipologia=Stand alone; Voltage-=220/240 V - 50/60 Hz - Stand alone; Weight (kg)=9.1; Weight (kg):=9,1; Working temperature=-25 +50 °C
- GWR5113V - ROAD5 MEDI HUGE V 3M 4000K 1,0A CL2: Body=Die-cast aluminium -; Catalogue Range=ROAD [5]; Classification:=-; Color Rendering Index=CRI-70; Colore=Graphite grey; Colour :=Powder coating; Colour temperature=4000K; Colour temperature:=4000 K (CRI>70); Context=Street and parking lighting; Control System=DALI - 5 Step; DIN 18032-3 certification=-; Descrizione=GWR5113V - ROAD5 MEDI HUGE V 3M 4000K 1,0A CL2; Device with reduced surface temperature=-; Driver=Included; Driver Box=Built-in; Efficiency (lm/W)=105; Electrocod=244C; Eletrical and lighting features=-; External screw=Stainless steel; Fixing=Pole Head - Outreach; Gasket=Anti-aging silicone; General information=-; Glow Wire Test :=-; IPEA=ROAD = A + // LARGE AREAS = A4 + // CYCLOPEDONALS = A + // GREEN AREAS = A + // HISTORICAL CENTER = A5 +; Installationa and maintenance=-; LED Life Time (L80B05)=120000H; LED Maintenance=Not available; LED current.=1A; Lamp-=LED; Lifetime=L90B10 (Tq+25°C) = 100.000 h - L90B10 (Tq+40°C) = 75.000 h; Locking Hook=Integrated front handle; Lumen output (lm)=12100; Luminaire=LED Road Equipment; Materials=-; Maximum surface exposed to the wind=0,149999999999999M2; Maximum surface exposed to the wind :=0.19 m2; Minimum distance from the illuminated object=1M; Modello=GWR5113V; Mouting and installation=Pole Head - Outreach; Nominal flux (lm)=14310; Number of modules=3 (3x3 LED); Operating temperature :=-25 +40 °C; Operating temperature:=-25 +40 °C; Optic=HUGE; Optic :=Metallized polycarbonate reflector; Optic Maintenance=Not available; Optic and illuminating features=-; Overvoltage protection=DM 10KV / CM 10KV; Photobiological Risk Class=RG0; Rated frequency (Hz)=50 / 60; SEO=Street lighting; Shield type=4mm thick flat tempered glass; Standard Deviation Colour Matching=SDCM = 5; Standard-=EN 60598-2-3, EN 60598-1 IEC/TR 62778; Standards and approvals=-; Stocking temperature=-; Supply voltage=220 - 240 V; System power=113W; System power :=115 W @ 1A; Tilt adjustable=-20° ÷ +10° side bracket - -10° ÷ +20° pole head; Tilt-=-20° ÷ +10° side bracket - -10° ÷ +20° pole head; Tipologia=Programmable (5 step); Type of light source=LED - Not replaceable; Unified Glare Rating=G*3 - ULOR = 0; Unique digital code (Datamatrix)=Currently not present; Voltage-=220/240 V - 50/60 Hz - Stand alone and/or programmable; Weight (kg):=8; Wiring=Isolating switch
- GWR5175M - ROAD5 MEDI HUGE 5M 4000K 0,7A CL2 1-10V: Catalogue Range=ROAD [5]; Colour temperature=4000 K (CRI 70); Colour temperature:=4000 K (CRI 70); Descrizione=ROAD 5 DIMM.5M 4000K 700mA OPT.ST1; EAN code=8011564858220; Electrocod=244C; LED LifeTime (L80B05)=77000H; LED current.=0,7A; Lamp-=LED; Lumen output (lm)=11480; Maximum surface exposed to the wind=0,19M2; Minimum distance from the illuminated object=1M; Modello=GWR5175M; No. Chorus modules=5 (5x3 LED); Nominal flux (lm)=15600; Number of modules=5 (5x3 LED); Operating temperature:=-25 +50 °C; Optic=H - ULOR: 0%; Overvoltage resistance=12 KV (Common and dfferential mode); Pilot current=0,7A; Power supply operation=Dimmable; SEO=Street lighting; System power=132W; Tilt adjustable=-20° ÷ +10° side bracket - -10° ÷ +20° pole head; Tipo alimentatore=Constant Current Driver Led; Tipologia=Dimmable; Voltage-=220/240 V - 50/60 Hz - Dimmable 1-10 V; Weight (kg)=8,8; Weight (kg):=8,8; Working temperature=-25 +50 °C
- GWR5173V - ROAD5 MEDI HUGE V 3M 4000K 0,7A CL2: Body=Die-cast aluminium -; Catalogue Range=ROAD [5]; Classification:=-; Color Rendering Index=CRI-70; Colore=Graphite grey; Colour :=Powder coating; Colour temperature=4000K; Colour temperature:=4000 K (CRI>70); Context=Street and parking lighting; Control System=DALI - 5 Step; DIN 18032-3 certification=-; Descrizione=GWR5173V - ROAD5 MEDI HUGE V 3M 4000K 0,7A CL2; Device with reduced surface temperature=-; Driver=Included; Driver Box=Built-in; Efficiency (lm/W)=111; Electrocod=244C; Eletrical and lighting features=-; External screw=Stainless steel; Fixing=Pole Head - Outreach; Gasket=Anti-aging silicone; General information=-; Glow Wire Test :=-; IPEA=ROAD = A3 + // LARGE AREAS = A4 + // CYCLOPEDONALS = A ++ // GREEN AREAS = A ++ // HISTORICAL CENTER = A6 +; Installationa and maintenance=-; LED Life Time (L80B05)=120000H; LED Maintenance=Not available; LED current.=0,7A; Lamp-=LED; Lifetime=L90B10 (Tq+25°C) = 100.000 h - L90B10 (Tq+50°C) = 75.000 h; Locking Hook=Integrated front handle; Lumen output (lm)=9000; Luminaire=LED Road Equipment; Materials=-; Maximum surface exposed to the wind=0,19M2; Maximum surface exposed to the wind :=0.19 m2; Minimum distance from the illuminated object=1M; Modello=GWR5173V; Mouting and installation=Pole Head - Outreach; Nominal flux (lm)=9360; Number of modules=3 (3x3 LED); Operating temperature :=-25 +50 °C; Operating temperature:=-25 +40 °C; Optic=HUGE; Optic :=Metallized polycarbonate reflector; Optic Maintenance=Not available; Optic and illuminating features=-; Overvoltage protection=DM 10KV / CM 10KV; Photobiological Risk Class=RG0; Rated frequency (Hz)=50 / 60; SEO=Street lighting; Shield type=4mm thick flat tempered glass; Standard Deviation Colour Matching=SDCM = 5; Standard-=EN 60598-2-3, EN 60598-1 IEC/TR 62778; Standards and approvals=-; Stocking temperature=-; Supply voltage=220 - 240 V; System power=79W; System power :=81 W @ 0.7A; Tilt adjustable=-20° ÷ +10° side bracket - -10° ÷ +20° pole head; Tilt-=-20° ÷ +10° side bracket - -10° ÷ +20° pole head; Tipologia=Programmable (5 step); Type of light source=LED - Not replaceable; Unified Glare Rating=G*3 - ULOR = 0; Unique digital code (Datamatrix)=Currently not present; Voltage-=220/240 V - 50/60 Hz - Stand alone and/or programmable; Weight (kg):=8; Wiring=Isolating switch
- GWR5176B30K - ROAD5 MEDI HUGE 6M 3000K 0,7A CL2 BIREG: Body=Die-cast aluminium -; Catalogue Range=ROAD [5]; Classification:=-; Color Rendering Index=CRI-70; Colore=Graphite grey; Colour :=Powder coating; Colour temperature=3000K; Colour temperature:=3000 K (CRI>80); Context=Street and parking lighting; Control System=Bi-power with self-learning; DIN 18032-3 certification=-; Descrizione=GWR5176B30K - ROAD5 MEDI HUGE 6M 3000K 0,7A CL2 BIREG; Device with reduced surface temperature=-; Driver=Included; Driver Box=Built-in; Efficiency (lm/W)=97; Electrocod=244C; Eletrical and lighting features=-; External screw=Stainless steel; Fixing=Pole Head - Outreach; Gasket=Anti-aging silicone; General information=-; Glow Wire Test :=-; IPEA=ROAD = B // LARGE AREAS = A ++ // CYCLOPEDONALS = A // GREEN AREAS = A // HISTORICAL CENTER = A3 +; Installationa and maintenance=-; LED Life Time (L80B05)=77000H; LED Maintenance=Not available; LED current.=0,7A; Lamp-=LED; Lifetime=L90B10 (Tq+25°C) = 100.000 h - L90B10 (Tq+50°C) = 50.000 h; Locking Hook=Integrated front handle; Lumen output (lm)=15600; Luminaire=LED Road Equipment; Materials=-; Maximum surface exposed to the wind=0,19M2; Maximum surface exposed to the wind :=0.19 m2; Minimum distance from the illuminated object=1M; Modello=GWR5176B30K; Mouting and installation=Pole Head - Outreach; Nominal flux (lm)=16200; Number of modules=6 (6x3 LED); Operating temperature :=-25 +50 °C; Operating temperature:=-25 +50 °C; Optic=HUGE; Optic :=Metallized polycarbonate reflector; Optic Maintenance=Not available; Optic and illuminating features=-; Overvoltage protection=DM 10KV / CM 10KV; Overvoltage resistance :=Common and dfferential mode: 10KV; Photobiological Risk Class=RG0; Power supply operation=Bi power; Rated frequency (Hz)=50 / 60; SEO=Street lighting; Shield type=4mm thick flat tempered glass; Standard Deviation Colour Matching=SDCM = 5; Standard-=EN 60598-2-3, EN 60598-1 IEC/TR 62778; Standards and approvals=-; Stocking temperature=-; Supply voltage=220 - 240 V; System power=161W; System power :=161 W @ 0.7A; Tilt adjustable=-20° ÷ +10° side bracket - -10° ÷ +20° pole head; Tilt-=-20° ÷ +10° side bracket - -10° ÷ +20° pole head; Tipo alimentatore=Constant Current Driver Led; Tipologia=Bi power; Type of light source=LED - Not replaceable; Unified Glare Rating=G*3 - ULOR = 0; Unique digital code (Datamatrix)=Currently not present; Voltage-=220/240 V - 50/60 Hz - Bi-power with self-learning; Weight (kg):=9,09999999999999; Wiring=Isolating switch
- GWR5116 - ROAD 5 6M 4000K 0,85A OPT.ST1: Catalogue Range=ROAD [5]; Colour temperature=4000 K (CRI 70); Colour temperature:=4000 K (CRI 70); Descrizione=ROAD 5 6M 4000K 0,85A OPT.ST1; EAN code=8011564857995; Electrocod=244C; LED LifeTime (L80B05)=120000H; LED current.=0,85A; Lamp-=LED; Lumen output (lm)=17160; Maximum surface exposed to the wind=0,19M2; Minimum distance from the illuminated object=1M; Modello=GWR5116; No. Chorus modules=6 (6x3 LED); Nominal flux (lm)=24330; Number of modules=6 (6x3 LED); Operating temperature:=-25 +40 °C; Optic=H - ULOR: 0%; Overvoltage resistance=12 KV (Common and dfferential mode); Pilot current=0,85A; SEO=Street lighting; System power=185W; Tilt adjustable=-20° ÷ +10° side bracket - -10° ÷ +20° pole head; Tipo alimentatore=Constant Current Driver Led; Tipologia=Stand alone; Voltage-=220/240 V - 50/60 Hz - Stand alone; Weight (kg)=9.1; Weight (kg):=9,1; Working temperature=-25 +40 °C
- GWR5153B - ROAD5 MEDI HUGE 3M 4000K 0,5A CL2 BIREG: Body=Die-cast aluminium -; Catalogue Range=ROAD [5]; Classification:=-; Color Rendering Index=CRI-70; Colore=Graphite grey; Colour :=Powder coating; Colour temperature=4000K; Colour temperature:=4000 K (CRI>70); Context=Street and parking lighting; Control System=Bi-power with self-learning; DIN 18032-3 certification=-; Descrizione=GWR5153B - ROAD5 MEDI HUGE 3M 4000K 0,5A CL2 BIREG; Device with reduced surface temperature=-; Driver=Included; Driver Box=Built-in; Efficiency (lm/W)=114; Electrocod=244C; Eletrical and lighting features=-; External screw=Stainless steel; Fixing=Pole Head - Outreach; Gasket=Anti-aging silicone; General information=-; Glow Wire Test :=-; IPEA=ROAD = A4 + // LARGE AREAS = A5 + // CYCLOPEDONALS = A4 + // GREEN AREAS = A4 + // HISTORICAL CENTER = A6 +; Installationa and maintenance=-; LED Life Time (L80B05)=120000H; LED Maintenance=Not available; LED current.=0,5A; Lamp-=LED; Lifetime=L90B10 (Tq+25°C) = 100.000 h - L90B10 (Tq+50°C) = 75.000 h; Locking Hook=Integrated front handle; Lumen output (lm)=6600; Luminaire=LED Road Equipment; Materials=-; Maximum surface exposed to the wind=0,19M2; Maximum surface exposed to the wind :=0.19 m2; Minimum distance from the illuminated object=1M; Modello=GWR5153B; Mouting and installation=Pole Head - Outreach; Nominal flux (lm)=7200; Number of modules=3 (3x3 LED); Operating temperature :=-25 +50 °C; Operating temperature:=-25 +40 °C; Optic=HUGE; Optic :=Metallized polycarbonate reflector; Optic Maintenance=Not available; Optic and illuminating features=-; Overvoltage protection=DM 10KV / CM 10KV; Photobiological Risk Class=RG0; Power supply operation=Bi power; Rated frequency (Hz)=50 / 60; SEO=Street lighting; Shield type=4mm thick flat tempered glass; Standard Deviation Colour Matching=SDCM = 5; Standard-=EN 60598-2-3, EN 60598-1 IEC/TR 62778; Standards and approvals=-; Stocking temperature=-; Supply voltage=220 - 240 V; System power=54W; System power :=58 W @ 0.5A; Tilt adjustable=-20° ÷ +10° side bracket - -10° ÷ +20° pole head; Tilt-=-20° ÷ +10° side bracket - -10° ÷ +20° pole head; Type of light source=LED - Not replaceable; Unified Glare Rating=G*3 - ULOR = 0; Unique digital code (Datamatrix)=Currently not present; Voltage-=220/240 V - 50/60 Hz - Bi-power with self-learning; Weight (kg):=8; Wiring=Isolating switch
- GWR517630K - ROAD5 MEDI HUGE 6M 3000K 0,7A CL2: Body=Die-cast aluminium -; Catalogue Range=ROAD [5]; Classification:=-; Color Rendering Index=CRI-70; Colore=Graphite grey; Colour :=Powder coating; Colour temperature=3000K; Colour temperature:=3000 K (CRI>80); Context=Street and parking lighting; Control System=Stand alone; DIN 18032-3 certification=-; Descrizione=GWR517630K - ROAD5 MEDI HUGE 6M 3000K 0,7A CL2; Device with reduced surface temperature=-; Driver=Included; Driver Box=Built-in; Efficiency (lm/W)=98; Electrocod=244C; Eletrical and lighting features=-; External screw=Stainless steel; Fixing=Pole Head - Outreach; Gasket=Anti-aging silicone; General information=-; Glow Wire Test :=-; IPEA=ROAD = B // LARGE AREAS = A ++ // CYCLOPEDONALS = A // GREEN AREAS = A // HISTORICAL CENTER = A4 +; Installationa and maintenance=-; LED Life Time (L80B05)=77000H; LED Maintenance=Not available; LED current.=0,7A; Lamp-=LED; Lifetime=L90B10 (Tq+25°C) = 100.000 h - L90B10 (Tq+50°C) = 50.000 h; Locking Hook=Integrated front handle; Lumen output (lm)=15600; Luminaire=LED Road Equipment; Materials=-; Maximum surface exposed to the wind=0,19M2; Maximum surface exposed to the wind :=0.19 m2; Minimum distance from the illuminated object=1M; Modello=GWR517630K; Mouting and installation=Pole Head - Outreach; Nominal flux (lm)=16200; Number of modules=6 (6x3 LED); Operating temperature :=-25 +50 °C; Operating temperature:=-25 +50 °C; Optic=HUGE; Optic :=Metallized polycarbonate reflector; Optic Maintenance=Not available; Optic and illuminating features=-; Overvoltage protection=DM 10KV / CM 10KV; Overvoltage resistance :=Common and dfferential mode: 10KV; Photobiological Risk Class=RG0; Rated frequency (Hz)=50 / 60; SEO=Street lighting; Shield type=4mm thick flat tempered glass; Standard Deviation Colour Matching=SDCM = 5; Standard-=EN 60598-2-3, EN 60598-1 IEC/TR 62778; Standards and approvals=-; Stocking temperature=-; Supply voltage=220 - 240 V; System power=159W; System power :=159 W @ 0.7A; Tilt adjustable=-20° ÷ +10° side bracket - -10° ÷ +20° pole head; Tilt-=-20° ÷ +10° side bracket - -10° ÷ +20° pole head; Tipo alimentatore=Constant Current Driver Led; Tipologia=Stand alone; Type of light source=LED - Not replaceable; Unified Glare Rating=G*3 - ULOR = 0; Unique digital code (Datamatrix)=Currently not present; Voltage-=220/240 V - 50/60 Hz - Stand alone; Weight (kg):=9,09999999999999; Wiring=Isolating switch
- GWR5175V - ROAD5 MEDI HUGE V 5M 4000K 0,7A CL2: Body=Die-cast aluminium -; Catalogue Range=ROAD [5]; Classification:=-; Color Rendering Index=CRI-70; Colore=Graphite grey; Colour :=Powder coating; Colour temperature=4000K; Colour temperature:=4000 K (CRI>70); Context=Street and parking lighting; Control System=DALI - 5 Step; DIN 18032-3 certification=-; Descrizione=GWR5175V - ROAD5 MEDI HUGE V 5M 4000K 0,7A CL2; Device with reduced surface temperature=-; Driver=Included; Driver Box=Built-in; Efficiency (lm/W)=111; Electrocod=244C; Eletrical and lighting features=-; External screw=Stainless steel; Fixing=Pole Head - Outreach; Gasket=Anti-aging silicone; General information=-; Glow Wire Test :=-; IPEA=ROAD = A + // LARGE AREAS = A4 + // CYCLOPEDONALS = A + // GREEN AREAS = A + // HISTORICAL CENTER = A6 +; Installationa and maintenance=-; LED Life Time (L80B05)=120000H; LED Maintenance=Not available; LED current.=0,7A; Lamp-=LED; Lifetime=L90B10 (Tq+25°C) = 100.000 h - L90B10 (Tq+50°C) = 50.000 h; Locking Hook=Integrated front handle; Lumen output (lm)=14900; Luminaire=LED Road Equipment; Materials=-; Maximum surface exposed to the wind=0,19M2; Maximum surface exposed to the wind :=0.19 m2; Minimum distance from the illuminated object=1M; Modello=GWR5175V; Mouting and installation=Pole Head - Outreach; Nominal flux (lm)=15600; Number of modules=5 (5x3 LED); Operating temperature :=-25 +50 °C; Operating temperature:=-25 +40 °C; Optic=HUGE; Optic :=Metallized polycarbonate reflector; Optic Maintenance=Not available; Optic and illuminating features=-; Overvoltage protection=DM 10KV / CM 10KV; Photobiological Risk Class=RG0; Rated frequency (Hz)=50 / 60; SEO=Street lighting; Shield type=4mm thick flat tempered glass; Standard Deviation Colour Matching=SDCM = 5; Standard-=EN 60598-2-3, EN 60598-1 IEC/TR 62778; Standards and approvals=-; Stocking temperature=-; Supply voltage=220 - 240 V; System power=132W; System power :=134 W @ 0.7A; Tilt adjustable=-20° ÷ +10° side bracket - -10° ÷ +20° pole head; Tilt-=-20° ÷ +10° side bracket - -10° ÷ +20° pole head; Tipologia=Programmable (5 step); Type of light source=LED - Not replaceable; Unified Glare Rating=G*3 - ULOR = 0; Unique digital code (Datamatrix)=Currently not present; Voltage-=220/240 V - 50/60 Hz - Stand alone and/or programmable; Weight (kg):=8,8; Wiring=Isolating switch
- GWR5116B30K - ROAD5 MEDI HUGE 6M 3000K 0,85A CL2 BIREG: Body=Die-cast aluminium -; Catalogue Range=ROAD [5]; Classification:=-; Color Rendering Index=CRI-70; Colore=Graphite grey; Colour :=Powder coating; Colour temperature=3000K; Colour temperature:=3000 K (CRI>80); Context=Street and parking lighting; Control System=Bi-power with self-learning; DIN 18032-3 certification=-; Descrizione=GWR5116B30K - ROAD5 MEDI HUGE 6M 3000K 0,85A CL2 BIREG; Device with reduced surface temperature=-; Driver=Included; Driver Box=Built-in; Efficiency (lm/W)=98; Electrocod=244C; Eletrical and lighting features=-; External screw=Stainless steel; Fixing=Pole Head - Outreach; Gasket=Anti-aging silicone; General information=-; Glow Wire Test :=-; IPEA=ROAD = B // LARGE AREAS = A ++ // CYCLOPEDONALS = B // GREEN AREAS = B // HISTORICAL CENTER = A3 +; Installationa and maintenance=-; LED Life Time (L80B05)=120000H; LED Maintenance=Not available; LED current.=0,849999999999999A; Lamp-=LED; Lifetime=L90B10 (Tq+25°C) = 100.000 h - L90B10 (Tq+40°C) = 50.000 h; Locking Hook=Integrated front handle; Lumen output (lm)=18400; Luminaire=LED Road Equipment; Materials=-; Maximum surface exposed to the wind=0,19M2; Maximum surface exposed to the wind :=0.19 m2; Minimum distance from the illuminated object=1M; Modello=GWR5116B30K; Mouting and installation=Pole Head - Outreach; Nominal flux (lm)=21114; Number of modules=6 (6x3 LED); Operating temperature :=-25 +40 °C; Operating temperature:=-25 +40 °C; Optic=HUGE; Optic :=Metallized polycarbonate reflector; Optic Maintenance=Not available; Optic and illuminating features=-; Overvoltage protection=DM 10KV / CM 10KV; Overvoltage resistance :=Common and dfferential mode: 10KV; Photobiological Risk Class=RG0; Power supply operation=Bi power; Rated frequency (Hz)=50 / 60; SEO=Street lighting; Shield type=4mm thick flat tempered glass; Standard Deviation Colour Matching=SDCM = 5; Standard-=EN 60598-2-3, EN 60598-1 IEC/TR 62778; Standards and approvals=-; Stocking temperature=-; Supply voltage=220 - 240 V; System power=187W; System power :=187 W @ 0.85A; Tilt adjustable=-20° ÷ +10° side bracket - -10° ÷ +20° pole head; Tilt-=-20° ÷ +10° side bracket - -10° ÷ +20° pole head; Tipo alimentatore=Constant Current Driver Led; Tipologia=Bi power; Type of light source=LED - Not replaceable; Unified Glare Rating=G*3 - ULOR = 0; Unique digital code (Datamatrix)=Currently not present; Voltage-=220/240 V - 50/60 Hz - Bi-power with self-learning; Weight (kg):=9,09999999999999; Wiring=Isolating switch
- GWR5116M30K - ROAD5 MEDI HUGE 6M 3000K 0,85A CL2 1-10V: Body=Die-cast aluminium -; Catalogue Range=ROAD [5]; Classification:=-; Color Rendering Index=CRI-70; Colore=Graphite grey; Colour :=Powder coating; Colour temperature=3000K; Colour temperature:=3000 K (CRI>80); Context=Street and parking lighting; Control System=Dimmable 1-10 V; DIN 18032-3 certification=-; Descrizione=GWR5116M30K - ROAD5 MEDI HUGE 6M 3000K 0,85A CL2 1-10V; Device with reduced surface temperature=-; Driver=Included; Driver Box=Built-in; Efficiency (lm/W)=98; Electrocod=244C; Eletrical and lighting features=-; External screw=Stainless steel; Fixing=Pole Head - Outreach; Gasket=Anti-aging silicone; General information=-; Glow Wire Test :=-; IPEA=ROAD = B // LARGE AREAS = A ++ // CYCLOPEDONALS = B // GREEN AREAS = B // HISTORICAL CENTER = A3 +; Installationa and maintenance=-; LED Life Time (L80B05)=120000H; LED Maintenance=Not available; LED current.=0,849999999999999A; Lamp-=LED; Lifetime=L90B10 (Tq+25°C) = 100.000 h - L90B10 (Tq+40°C) = 50.000 h; Locking Hook=Integrated front handle; Lumen output (lm)=18400; Luminaire=LED Road Equipment; Materials=-; Maximum surface exposed to the wind=0,19M2; Maximum surface exposed to the wind :=0.19 m2; Minimum distance from the illuminated object=1M; Modello=GWR5116M30K; Mouting and installation=Pole Head - Outreach; Nominal flux (lm)=21114; Number of modules=6 (6x3 LED); Operating temperature :=-25 +40 °C; Operating temperature:=-25 +40 °C; Optic=HUGE; Optic :=Metallized polycarbonate reflector; Optic Maintenance=Not available; Optic and illuminating features=-; Overvoltage protection=DM 10KV / CM 10KV; Overvoltage resistance :=Common and dfferential mode: 10KV; Photobiological Risk Class=RG0; Power supply operation=Dimmable; Rated frequency (Hz)=50 / 60; SEO=Street lighting; Shield type=4mm thick flat tempered glass; Standard Deviation Colour Matching=SDCM = 5; Standard-=EN 60598-2-3, EN 60598-1 IEC/TR 62778; Standards and approvals=-; Stocking temperature=-; Supply voltage=220 - 240 V; System power=185W; System power :=187 W @ 0.85A; Tilt adjustable=-20° ÷ +10° side bracket - -10° ÷ +20° pole head; Tilt-=-20° ÷ +10° side bracket - -10° ÷ +20° pole head; Tipo alimentatore=Constant Current Driver Led; Tipologia=Dimmable; Type of light source=LED - Not replaceable; Unified Glare Rating=G*3 - ULOR = 0; Unique digital code (Datamatrix)=Currently not present; Voltage-=220/240 V - 50/60 Hz - Dimmable 1-10 V; Weight (kg):=9,09999999999999; Wiring=Isolating switch
- GWR5156B - ROAD5 MEDI HUGE 6M 4000K 0,5A CL2 BIREG: Body=Die-cast aluminium -; Catalogue Range=ROAD [5]; Classification:=-; Color Rendering Index=CRI-70; Colore=Graphite grey; Colour :=Powder coating; Colour temperature=4000K; Colour temperature:=4000 K (CRI>70); Context=Street and parking lighting; Control System=Bi-power with self-learning; DIN 18032-3 certification=-; Descrizione=GWR5156B - ROAD5 MEDI HUGE 6M 4000K 0,5A CL2 BIREG; Device with reduced surface temperature=-; Driver=Included; Driver Box=Built-in; Efficiency (lm/W)=117; Electrocod=244C; Eletrical and lighting features=-; External screw=Stainless steel; Fixing=Pole Head - Outreach; Gasket=Anti-aging silicone; General information=-; Glow Wire Test :=-; IPEA=ROAD = A3 + // LARGE AREAS = A5 + // CYCLOPEDONALS = A ++ // GREEN AREAS = A ++ // HISTORICAL CENTER = A6 +; Installationa and maintenance=-; LED Life Time (L80B05)=120000H; LED Maintenance=Not available; LED current.=0,5A; Lamp-=LED; Lifetime=L90B10 (Tq+25°C) = 100.000 h - L90B10 (Tq+50°C) = 50.000 h; Locking Hook=Integrated front handle; Lumen output (lm)=13200; Luminaire=LED Road Equipment; Materials=-; Maximum surface exposed to the wind=0,19M2; Maximum surface exposed to the wind :=0.19 m2; Minimum distance from the illuminated object=1M; Modello=GWR5156B; Mouting and installation=Pole Head - Outreach; Nominal flux (lm)=14400; Number of modules=6 (6x3 LED); Operating temperature :=-25 +50 °C; Operating temperature:=-25 +40 °C; Optic=HUGE; Optic :=Metallized polycarbonate reflector; Optic Maintenance=Not available; Optic and illuminating features=-; Overvoltage protection=DM 10KV / CM 10KV; Photobiological Risk Class=RG0; Power supply operation=Bi power; Rated frequency (Hz)=50 / 60; SEO=Street lighting; Shield type=4mm thick flat tempered glass; Standard Deviation Colour Matching=SDCM = 5; Standard-=EN 60598-2-3, EN 60598-1 IEC/TR 62778; Standards and approvals=-; Stocking temperature=-; Supply voltage=220 - 240 V; System power=109W; System power :=113 W @ 0.5A; Tilt adjustable=-20° ÷ +10° side bracket - -10° ÷ +20° pole head; Tilt-=-20° ÷ +10° side bracket - -10° ÷ +20° pole head; Type of light source=LED - Not replaceable; Unified Glare Rating=G*3 - ULOR = 0; Unique digital code (Datamatrix)=Currently not present; Voltage-=220/240 V - 50/60 Hz - Bi-power with self-learning; Weight (kg):=9,09999999999999; Wiring=Isolating switch
- GWR5115M30K - ROAD5 MEDI HUGE 5M 3000K 0,85A CL2 1-10V: Body=Die-cast aluminium -; Catalogue Range=ROAD [5]; Classification:=-; Color Rendering Index=CRI-70; Colore=Graphite grey; Colour :=Powder coating; Colour temperature=3000K; Colour temperature:=3000 K (CRI>80); Context=Street and parking lighting; Control System=Dimmable 1-10 V; DIN 18032-3 certification=-; Descrizione=GWR5115M30K - ROAD5 MEDI HUGE 5M 3000K 0,85A CL2 1-10V; Device with reduced surface temperature=-; Driver=Included; Driver Box=Built-in; Efficiency (lm/W)=95; Electrocod=244C; Eletrical and lighting features=-; External screw=Stainless steel; Fixing=Pole Head - Outreach; Gasket=Anti-aging silicone; General information=-; Glow Wire Test :=-; IPEA=ROAD = B // LARGE AREAS = A ++ // CYCLOPEDONALS = B // GREEN AREAS = B // HISTORICAL CENTER = A3 +; Installationa and maintenance=-; LED Life Time (L80B05)=120000H; LED Maintenance=Not available; LED current.=0,849999999999999A; Lamp-=LED; Lifetime=L90B10 (Tq+25°C) = 100.000 h - L90B10 (Tq+40°C) = 50.000 h; Locking Hook=Integrated front handle; Lumen output (lm)=15300; Luminaire=LED Road Equipment; Materials=-; Maximum surface exposed to the wind=0,19M2; Maximum surface exposed to the wind :=0.19 m2; Minimum distance from the illuminated object=1M; Modello=GWR5115M30K; Mouting and installation=Pole Head - Outreach; Nominal flux (lm)=18423; Number of modules=5 (5x3 LED); Operating temperature :=-25 +40 °C; Operating temperature:=-25 +40 °C; Optic=HUGE; Optic :=Metallized polycarbonate reflector; Optic Maintenance=Not available; Optic and illuminating features=-; Overvoltage protection=DM 10KV / CM 10KV; Overvoltage resistance :=Common and dfferential mode: 10KV; Photobiological Risk Class=RG0; Power supply operation=Dimmable; Rated frequency (Hz)=50 / 60; SEO=Street lighting; Shield type=4mm thick flat tempered glass; Standard Deviation Colour Matching=SDCM = 5; Standard-=EN 60598-2-3, EN 60598-1 IEC/TR 62778; Standards and approvals=-; Stocking temperature=-; Supply voltage=220 - 240 V; System power=159W; System power :=161 W @ 0.85A; Tilt adjustable=-20° ÷ +10° side bracket - -10° ÷ +20° pole head; Tilt-=-20° ÷ +10° side bracket - -10° ÷ +20° pole head; Tipo alimentatore=Constant Current Driver Led; Tipologia=Dimmable; Type of light source=LED - Not replaceable; Unified Glare Rating=G*3 - ULOR = 0; Unique digital code (Datamatrix)=Currently not present; Voltage-=220/240 V - 50/60 Hz - Dimmable 1-10 V; Weight (kg):=8,8; Wiring=Isolating switch
- GWR5175B30K - ROAD5 MEDI HUGE 5M 3000K 0,7A CL2 BIREG: Body=Die-cast aluminium -; Catalogue Range=ROAD [5]; Classification:=-; Color Rendering Index=CRI-70; Colore=Graphite grey; Colour :=Powder coating; Colour temperature=3000K; Colour temperature:=3000 K (CRI>80); Context=Street and parking lighting; Control System=Bi-power with self-learning; DIN 18032-3 certification=-; Descrizione=GWR5175B30K - ROAD5 MEDI HUGE 5M 3000K 0,7A CL2 BIREG; Device with reduced surface temperature=-; Driver=Included; Driver Box=Built-in; Efficiency (lm/W)=97; Electrocod=244C; Eletrical and lighting features=-; External screw=Stainless steel; Fixing=Pole Head - Outreach; Gasket=Anti-aging silicone; General information=-; Glow Wire Test :=-; IPEA=ROAD = B // LARGE AREAS = A ++ // CYCLOPEDONALS = A // GREEN AREAS = A // HISTORICAL CENTER = A3 +; Installationa and maintenance=-; LED Life Time (L80B05)=77000H; LED Maintenance=Not available; LED current.=0,7A; Lamp-=LED; Lifetime=L90B10 (Tq+25°C) = 100.000 h - L90B10 (Tq+50°C) = 50.000 h; Locking Hook=Integrated front handle; Lumen output (lm)=13000; Luminaire=LED Road Equipment; Materials=-; Maximum surface exposed to the wind=0,19M2; Maximum surface exposed to the wind :=0.19 m2; Minimum distance from the illuminated object=1M; Modello=GWR5175B30K; Mouting and installation=Pole Head - Outreach; Nominal flux (lm)=13500; Number of modules=5 (5x3 LED); Operating temperature :=-25 +50 °C; Operating temperature:=-25 +50 °C; Optic=HUGE; Optic :=Metallized polycarbonate reflector; Optic Maintenance=Not available; Optic and illuminating features=-; Overvoltage protection=DM 10KV / CM 10KV; Overvoltage resistance :=Common and dfferential mode: 10KV; Photobiological Risk Class=RG0; Power supply operation=Bi power; Rated frequency (Hz)=50 / 60; SEO=Street lighting; Shield type=4mm thick flat tempered glass; Standard Deviation Colour Matching=SDCM = 5; Standard-=EN 60598-2-3, EN 60598-1 IEC/TR 62778; Standards and approvals=-; Stocking temperature=-; Supply voltage=220 - 240 V; System power=134W; System power :=134 W @ 0.7A; Tilt adjustable=-20° ÷ +10° side bracket - -10° ÷ +20° pole head; Tilt-=-20° ÷ +10° side bracket - -10° ÷ +20° pole head; Tipo alimentatore=Constant Current Driver Led; Tipologia=Bi power; Type of light source=LED - Not replaceable; Unified Glare Rating=G*3 - ULOR = 0; Unique digital code (Datamatrix)=Currently not present; Voltage-=220/240 V - 50/60 Hz - Bi-power with self-learning; Weight (kg):=8,8; Wiring=Isolating switch
- GWR5175B - ROAD5 MEDI HUGE 5M 4000K 0,7A CL2 BIREG: Catalogue Range=ROAD [5]; Colour temperature=4000 K (CRI 70); Colour temperature:=4000 K (CRI 70); Descrizione=ROAD 5 BI-POW.5M 4000K 700mA OPT.ST1; EAN code=8011564858046; Electrocod=244C; LED LifeTime (L80B05)=77000H; LED current.=0,7A; Lamp-=LED; Lumen output (lm)=11480; Maximum surface exposed to the wind=0,19M2; Minimum distance from the illuminated object=1M; Modello=GWR5175B; No. Chorus modules=5 (5x3 LED); Nominal flux (lm)=15600; Number of modules=5 (5x3 LED); Operating temperature:=-25 +50 °C; Optic=H - ULOR: 0%; Overvoltage resistance=12 KV (Common and dfferential mode); Pilot current=0,7A; Power supply operation=Bi power; SEO=Street lighting; System power=134W; Tilt adjustable=-20° ÷ +10° side bracket - -10° ÷ +20° pole head; Tipo alimentatore=Constant Current Driver Led; Tipologia=Bi power; Voltage-=220/240 V - 50/60 Hz - Bi-power with self-learning; Weight (kg)=8,8; Weight (kg):=8,8; Working temperature=-25 +50 °C
- GWR5115 - ROAD 5 5M 4000K 0,85A OPT.ST1: Catalogue Range=ROAD [5]; Colour temperature=4000 K (CRI 70); Colour temperature:=4000 K (CRI 70); Descrizione=ROAD 5 5M 4000K 0,85A OPT.ST1; EAN code=8011564857971; Electrocod=244C; LED LifeTime (L80B05)=120000H; LED current.=0,85A; Lamp-=LED; Lumen output (lm)=14970; Maximum surface exposed to the wind=0,19M2; Minimum distance from the illuminated object=1M; Modello=GWR5115; No. Chorus modules=5 (5x3 LED); Nominal flux (lm)=21230; Number of modules=5 (5x3 LED); Operating temperature:=-25 +40 °C; Optic=H - ULOR: 0%; Overvoltage resistance=12 KV (Common and dfferential mode); Pilot current=0,85A; SEO=Street lighting; System power=159W; Tilt adjustable=-20° ÷ +10° side bracket - -10° ÷ +20° pole head; Tipo alimentatore=Constant Current Driver Led; Tipologia=Stand alone; Voltage-=220/240 V - 50/60 Hz - Stand alone; Weight (kg)=8,8; Weight (kg):=8,8; Working temperature=-25 +40 °C
- GWR5114V - ROAD5 MEDI HUGE V 4M 4000K 1,0A CL2: Body=Die-cast aluminium -; Catalogue Range=ROAD [5]; Classification:=-; Color Rendering Index=CRI-70; Colore=Graphite grey; Colour :=Powder coating; Colour temperature=4000K; Colour temperature:=4000 K (CRI>70); Context=Street and parking lighting; Control System=DALI - 5 Step; DIN 18032-3 certification=-; Descrizione=GWR5114V - ROAD5 MEDI HUGE V 4M 4000K 1,0A CL2; Device with reduced surface temperature=-; Driver=Included; Driver Box=Built-in; Efficiency (lm/W)=105; Electrocod=244C; Eletrical and lighting features=-; External screw=Stainless steel; Fixing=Pole Head - Outreach; Gasket=Anti-aging silicone; General information=-; Glow Wire Test :=-; IPEA=ROAD = A // LARGE AREAS = A3 + // CYCLOPEDONALS = A // GREEN AREAS = A // HISTORICAL CENTER = A5 +; Installationa and maintenance=-; LED Life Time (L80B05)=120000H; LED Maintenance=Not available; LED current.=1A; Lamp-=LED; Lifetime=L90B10 (Tq+25°C) = 100.000 h - L90B10 (Tq+40°C) = 50.000 h; Locking Hook=Integrated front handle; Lumen output (lm)=16100; Luminaire=LED Road Equipment; Materials=-; Maximum surface exposed to the wind=0,19M2; Maximum surface exposed to the wind :=0.19 m2; Minimum distance from the illuminated object=1M; Modello=GWR5114V; Mouting and installation=Pole Head - Outreach; Nominal flux (lm)=19080; Number of modules=4 (4x3 LED); Operating temperature :=-25 +40 °C; Operating temperature:=-25 +40 °C; Optic=HUGE; Optic :=Metallized polycarbonate reflector; Optic Maintenance=Not available; Optic and illuminating features=-; Overvoltage protection=DM 10KV / CM 10KV; Photobiological Risk Class=RG0; Rated frequency (Hz)=50 / 60; SEO=Street lighting; Shield type=4mm thick flat tempered glass; Standard Deviation Colour Matching=SDCM = 5; Standard-=EN 60598-2-3, EN 60598-1 IEC/TR 62778; Standards and approvals=-; Stocking temperature=-; Supply voltage=220 - 240 V; System power=151W; System power :=153 W @ 1A; Tilt adjustable=-20° ÷ +10° side bracket - -10° ÷ +20° pole head; Tilt-=-20° ÷ +10° side bracket - -10° ÷ +20° pole head; Tipologia=Programmable (5 step); Type of light source=LED - Not replaceable; Unified Glare Rating=G*3 - ULOR = 0; Unique digital code (Datamatrix)=Currently not present; Voltage-=220/240 V - 50/60 Hz - Stand alone and/or programmable; Weight (kg):=8,4; Wiring=Isolating switch
- GWR5174M - ROAD5 MEDI HUGE 4M 4000K 0,7A CL2 1-10V: Catalogue Range=ROAD [5]; Colour temperature=4000 K (CRI 70); Colour temperature:=4000 K (CRI 70); Descrizione=ROAD 5 DIMM.4M 4000K 700mA OPT.ST1; EAN code=8011564858107; Electrocod=244C; LED LifeTime (L80B05)=77000H; LED current.=0,7A; Lamp-=LED; Lumen output (lm)=9190; Maximum surface exposed to the wind=0,19M2; Minimum distance from the illuminated object=1M; Modello=GWR5174M; No. Chorus modules=4 (4x3 LED); Nominal flux (lm)=12480; Number of modules=4 (4x3 LED); Operating temperature:=-25 +50 °C; Optic=H - ULOR: 0%; Overvoltage resistance=12 KV (Common and dfferential mode); Pilot current=0,7A; Power supply operation=Dimmable; SEO=Street lighting; System power=106W; Tilt adjustable=-20° ÷ +10° side bracket - -10° ÷ +20° pole head; Tipo alimentatore=Constant Current Driver Led; Tipologia=Dimmable; Voltage-=220/240 V - 50/60 Hz - Dimmable 1-10 V; Weight (kg)=8,4; Weight (kg):=8,4; Working temperature=-25 +50 °C
- GWR511430K - ROAD5 MEDI HUGE 4M 3000K 1,0A CL2: Body=Die-cast aluminium -; Catalogue Range=ROAD [5]; Classification:=-; Color Rendering Index=CRI-70; Colore=Graphite grey; Colour :=Powder coating; Colour temperature=3000K; Colour temperature:=3000 K (CRI>80); Context=Street and parking lighting; Control System=Stand alone; DIN 18032-3 certification=-; Descrizione=GWR511430K - ROAD5 MEDI HUGE 4M 3000K 1,0A CL2; Device with reduced surface temperature=-; Driver=Included; Driver Box=Built-in; Efficiency (lm/W)=93; Electrocod=244C; Eletrical and lighting features=-; External screw=Stainless steel; Fixing=Pole Head - Outreach; Gasket=Anti-aging silicone; General information=-; Glow Wire Test :=-; IPEA=ROAD = B // LARGE AREAS = A + // CYCLOPEDONALS = B // GREEN AREAS = B // HISTORICAL CENTER = A3 +; Installationa and maintenance=-; LED Life Time (L80B05)=120000H; LED Maintenance=Not available; LED current.=1A; Lamp-=LED; Lifetime=L90B10 (Tq+25°C) = 100.000 h - L90B10 (Tq+40°C) = 50.000 h; Locking Hook=Integrated front handle; Lumen output (lm)=14000; Luminaire=LED Road Equipment; Materials=-; Maximum surface exposed to the wind=0,19M2; Maximum surface exposed to the wind :=0.19 m2; Minimum distance from the illuminated object=1M; Modello=GWR511430K; Mouting and installation=Pole Head - Outreach; Nominal flux (lm)=16560; Number of modules=4 (4x3 LED); Operating temperature :=-25 +40 °C; Operating temperature:=-25 +40 °C; Optic=HUGE; Optic :=Metallized polycarbonate reflector; Optic Maintenance=Not available; Optic and illuminating features=-; Overvoltage protection=DM 10KV / CM 10KV; Overvoltage resistance :=Common and dfferential mode: 10KV; Photobiological Risk Class=RG0; Rated frequency (Hz)=50 / 60; SEO=Street lighting; Shield type=4mm thick flat tempered glass; Standard Deviation Colour Matching=SDCM = 5; Standard-=EN 60598-2-3, EN 60598-1 IEC/TR 62778; Standards and approvals=-; Stocking temperature=-; Supply voltage=220 - 240 V; System power=151W; System power :=151 W @ 1A; Tilt adjustable=-20° ÷ +10° side bracket - -10° ÷ +20° pole head; Tilt-=-20° ÷ +10° side bracket - -10° ÷ +20° pole head; Tipo alimentatore=Constant Current Driver Led; Tipologia=Stand alone; Type of light source=LED - Not replaceable; Unified Glare Rating=G*3 - ULOR = 0; Unique digital code (Datamatrix)=Currently not present; Voltage-=220/240 V - 50/60 Hz - Stand alone; Weight (kg):=8,4; Wiring=Isolating switch
- GWR5116V - ROAD5 MEDI HUGE V 6M 4000K 0,85A CL2: Body=Die-cast aluminium -; Catalogue Range=ROAD [5]; Classification:=-; Color Rendering Index=CRI-70; Colore=Graphite grey; Colour :=Powder coating; Colour temperature=4000K; Colour temperature:=4000 K (CRI>70); Context=Street and parking lighting; Control System=DALI - 5 Step; DIN 18032-3 certification=-; Descrizione=GWR5116V - ROAD5 MEDI HUGE V 6M 4000K 0,85A CL2; Device with reduced surface temperature=-; Driver=Included; Driver Box=Built-in; Efficiency (lm/W)=113; Electrocod=244C; Eletrical and lighting features=-; External screw=Stainless steel; Fixing=Pole Head - Outreach; Gasket=Anti-aging silicone; General information=-; Glow Wire Test :=-; IPEA=ROAD = A // LARGE AREAS = A4 + // CYCLOPEDONALS = A + // GREEN AREAS = A + // HISTORICAL CENTER = A5 +; Installationa and maintenance=-; LED Life Time (L80B05)=120000H; LED Maintenance=Not available; LED current.=0,849999999999999A; Lamp-=LED; Lifetime=L90B10 (Tq+25°C) = 100.000 h - L90B10 (Tq+40°C) = 50.000 h; Locking Hook=Integrated front handle; Lumen output (lm)=21100; Luminaire=LED Road Equipment; Materials=-; Maximum surface exposed to the wind=0,19M2; Maximum surface exposed to the wind :=0.19 m2; Minimum distance from the illuminated object=1M; Modello=GWR5116V; Mouting and installation=Pole Head - Outreach; Nominal flux (lm)=24330; Number of modules=6 (6x3 LED); Operating temperature :=-25 +40 °C; Operating temperature:=-25 +40 °C; Optic=HUGE; Optic :=Metallized polycarbonate reflector; Optic Maintenance=Not available; Optic and illuminating features=-; Overvoltage protection=DM 10KV / CM 10KV; Photobiological Risk Class=RG0; Rated frequency (Hz)=50 / 60; SEO=Street lighting; Shield type=4mm thick flat tempered glass; Standard Deviation Colour Matching=SDCM = 5; Standard-=EN 60598-2-3, EN 60598-1 IEC/TR 62778; Standards and approvals=-; Stocking temperature=-; Supply voltage=220 - 240 V; System power=185W; System power :=187 W @ 0.85A; Tilt adjustable=-20° ÷ +10° side bracket - -10° ÷ +20° pole head; Tilt-=-20° ÷ +10° side bracket - -10° ÷ +20° pole head; Tipologia=Programmable (5 step); Type of light source=LED - Not replaceable; Unified Glare Rating=G*3 - ULOR = 0; Unique digital code (Datamatrix)=Currently not present; Voltage-=220/240 V - 50/60 Hz - Stand alone and/or programmable; Weight (kg):=9,09999999999999; Wiring=Isolating switch

## geometry (parser evidence)
native form markers: Blend x2
no freeform markers — native parametric forms only
